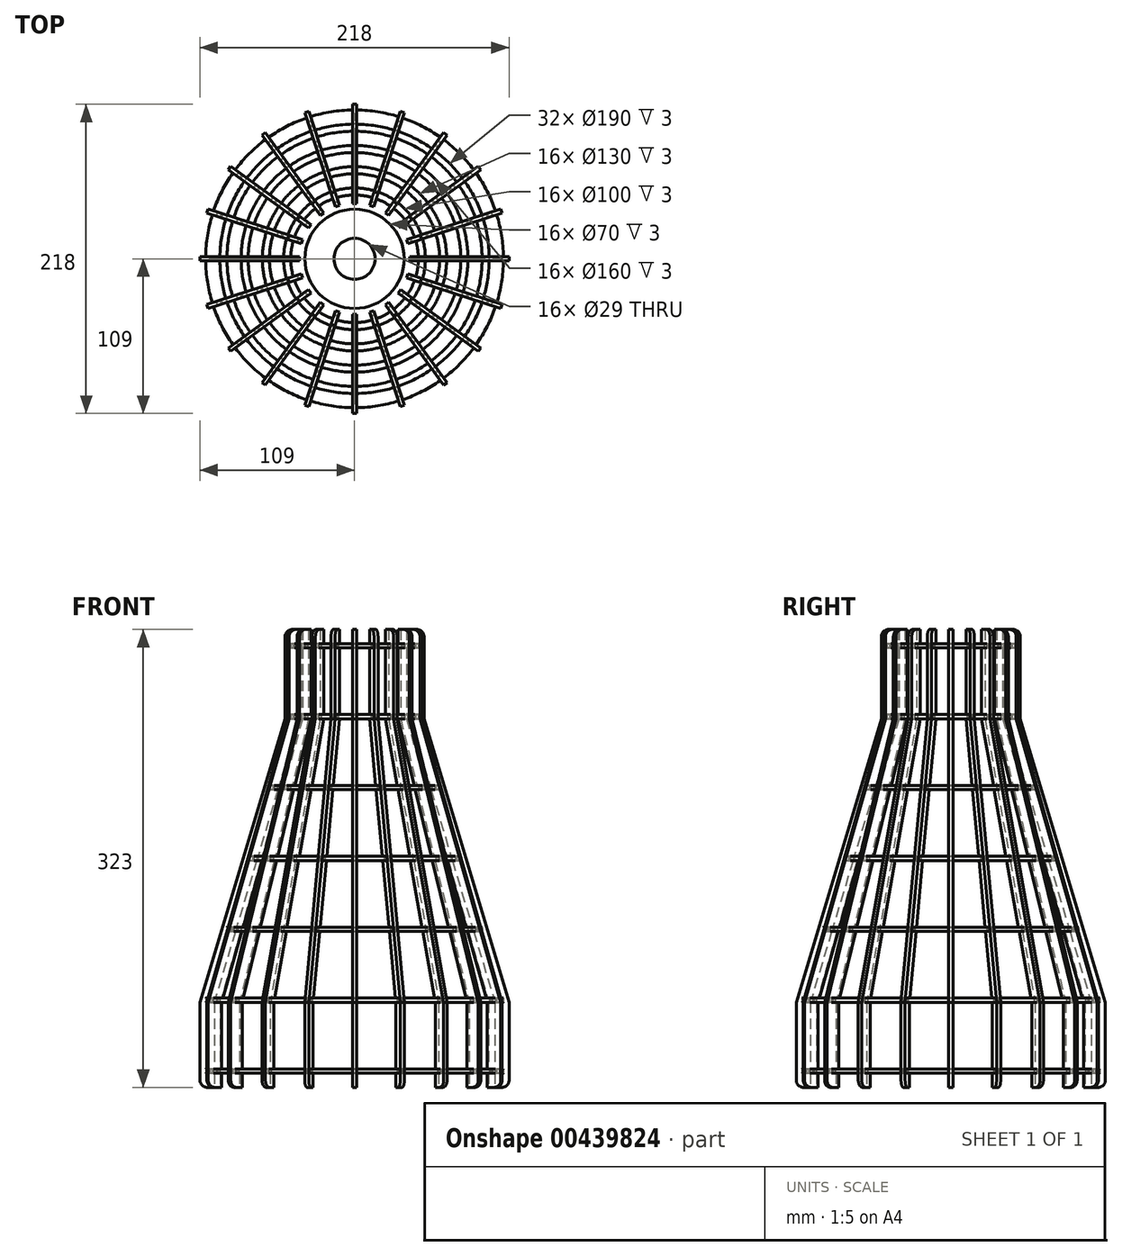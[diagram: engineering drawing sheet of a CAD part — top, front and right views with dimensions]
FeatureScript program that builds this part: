
annotation { "Feature Type Name" : "Feature", "Feature Type Description" : "" }
export const myFeature = defineFeature(function(context is Context, id is Id, definition is map)
    precondition{}
    {
        {
            var Q0;
            Q0=qCreatedBy(makeId("Top.planeOp"),FACE);
            cPlane(context, id + "F0", {"entities" : qUnion([Q0]), "cplaneType" : CPlaneType.OFFSET, "offset" : 50 * mm, "width" : 150 * mm, "height" : 150 * mm});
        }
        {
            var Q0;
            Q0=qCreatedBy(id+"F0.planeOp",FACE);
            cPlane(context, id + "F1", {"entities" : qUnion([Q0]), "cplaneType" : CPlaneType.OFFSET, "offset" : 50 * mm, "width" : 150 * mm, "height" : 150 * mm});
        }
        {
            var Q0;
            Q0=qCreatedBy(id+"F1.planeOp",FACE);
            cPlane(context, id + "F2", {"entities" : qUnion([Q0]), "cplaneType" : CPlaneType.OFFSET, "offset" : 50 * mm, "width" : 150 * mm, "height" : 150 * mm});
        }
        {
            var Q0;
            Q0=qCreatedBy(makeId("Top.planeOp"),FACE);
            cPlane(context, id + "F3", {"entities" : qUnion([Q0]), "cplaneType" : CPlaneType.OFFSET, "offset" : 50 * mm, "oppositeDirection" : true, "width" : 150 * mm, "height" : 150 * mm});
        }
        {
            var Q0;
            Q0=qCreatedBy(id+"F3.planeOp",FACE);
            cPlane(context, id + "F4", {"entities" : qUnion([Q0]), "cplaneType" : CPlaneType.OFFSET, "offset" : 50 * mm, "oppositeDirection" : true, "width" : 150 * mm, "height" : 150 * mm});
        }
        {
            var Q0;
            Q0=qCreatedBy(id+"F4.planeOp",FACE);
            cPlane(context, id + "F5", {"entities" : qUnion([Q0]), "cplaneType" : CPlaneType.OFFSET, "offset" : 50 * mm, "oppositeDirection" : true, "width" : 150 * mm, "height" : 150 * mm});
        }
        {
            var Q0;
            Q0=qCreatedBy(id+"F2.planeOp",FACE);
            var sketch = newSketch(context, id + "F6", { "sketchPlane" : qUnion([Q0])});
            skCircle(sketch, "E0", {"center": v(0, 0) * mm, "radius": 35 * mm});
            skArc(sketch, "E1", {"start": v(-44.98, -1.4) * mm, "mid": v(-44.45, -7.04) * mm, "end": v(-43.2, -12.57) * mm});
            skLineSegment(sketch, "E2", {"start": v(-44.98, 1.4) * mm, "end": v(-42, 1.4) * mm});
            skLineSegment(sketch, "E3", {"start": v(-42, 1.4) * mm, "end": v(-42, -1.4) * mm});
            skLineSegment(sketch, "E4", {"start": v(-42, -1.4) * mm, "end": v(-44.98, -1.4) * mm});
            skLineSegment(sketch, "E5.1.0", {"start": v(-43.2, -12.57) * mm, "end": v(-40.38, -11.65) * mm});
            skLineSegment(sketch, "E5.1.1", {"start": v(-40.38, -11.65) * mm, "end": v(-39.51, -14.31) * mm});
            skLineSegment(sketch, "E5.1.2", {"start": v(-39.51, -14.31) * mm, "end": v(-42.34, -15.23) * mm});
            skLineSegment(sketch, "E5.2.0", {"start": v(-37.21, -25.3) * mm, "end": v(-34.8, -23.55) * mm});
            skLineSegment(sketch, "E5.2.1", {"start": v(-34.8, -23.55) * mm, "end": v(-33.16, -25.82) * mm});
            skLineSegment(sketch, "E5.2.2", {"start": v(-33.16, -25.82) * mm, "end": v(-35.57, -27.57) * mm});
            skLineSegment(sketch, "E5.3.0", {"start": v(-27.57, -35.57) * mm, "end": v(-25.82, -33.16) * mm});
            skLineSegment(sketch, "E5.3.1", {"start": v(-25.82, -33.16) * mm, "end": v(-23.55, -34.8) * mm});
            skLineSegment(sketch, "E5.3.2", {"start": v(-23.55, -34.8) * mm, "end": v(-25.3, -37.21) * mm});
            skLineSegment(sketch, "E5.4.0", {"start": v(-15.23, -42.34) * mm, "end": v(-14.31, -39.51) * mm});
            skLineSegment(sketch, "E5.4.1", {"start": v(-14.31, -39.51) * mm, "end": v(-11.65, -40.38) * mm});
            skLineSegment(sketch, "E5.4.2", {"start": v(-11.65, -40.38) * mm, "end": v(-12.57, -43.2) * mm});
            skLineSegment(sketch, "E5.5.0", {"start": v(-1.4, -44.98) * mm, "end": v(-1.4, -42) * mm});
            skLineSegment(sketch, "E5.5.1", {"start": v(-1.4, -42) * mm, "end": v(1.4, -42) * mm});
            skLineSegment(sketch, "E5.5.2", {"start": v(1.4, -42) * mm, "end": v(1.4, -44.98) * mm});
            skLineSegment(sketch, "E5.6.0", {"start": v(12.57, -43.2) * mm, "end": v(11.65, -40.38) * mm});
            skLineSegment(sketch, "E5.6.1", {"start": v(11.65, -40.38) * mm, "end": v(14.31, -39.51) * mm});
            skLineSegment(sketch, "E5.6.2", {"start": v(14.31, -39.51) * mm, "end": v(15.23, -42.34) * mm});
            skLineSegment(sketch, "E5.7.0", {"start": v(25.3, -37.21) * mm, "end": v(23.55, -34.8) * mm});
            skLineSegment(sketch, "E5.7.1", {"start": v(23.55, -34.8) * mm, "end": v(25.82, -33.16) * mm});
            skLineSegment(sketch, "E5.7.2", {"start": v(25.82, -33.16) * mm, "end": v(27.57, -35.57) * mm});
            skLineSegment(sketch, "E5.8.0", {"start": v(35.57, -27.57) * mm, "end": v(33.16, -25.82) * mm});
            skLineSegment(sketch, "E5.8.1", {"start": v(33.16, -25.82) * mm, "end": v(34.8, -23.55) * mm});
            skLineSegment(sketch, "E5.8.2", {"start": v(34.8, -23.55) * mm, "end": v(37.21, -25.3) * mm});
            skLineSegment(sketch, "E5.9.0", {"start": v(42.34, -15.23) * mm, "end": v(39.51, -14.31) * mm});
            skLineSegment(sketch, "E5.9.1", {"start": v(39.51, -14.31) * mm, "end": v(40.38, -11.65) * mm});
            skLineSegment(sketch, "E5.9.2", {"start": v(40.38, -11.65) * mm, "end": v(43.2, -12.57) * mm});
            skLineSegment(sketch, "E5.10.0", {"start": v(44.98, -1.4) * mm, "end": v(42, -1.4) * mm});
            skLineSegment(sketch, "E5.10.1", {"start": v(42, -1.4) * mm, "end": v(42, 1.4) * mm});
            skLineSegment(sketch, "E5.10.2", {"start": v(42, 1.4) * mm, "end": v(44.98, 1.4) * mm});
            skLineSegment(sketch, "E5.11.0", {"start": v(43.2, 12.57) * mm, "end": v(40.38, 11.65) * mm});
            skLineSegment(sketch, "E5.11.1", {"start": v(40.38, 11.65) * mm, "end": v(39.51, 14.31) * mm});
            skLineSegment(sketch, "E5.11.2", {"start": v(39.51, 14.31) * mm, "end": v(42.34, 15.23) * mm});
            skLineSegment(sketch, "E5.12.0", {"start": v(37.21, 25.3) * mm, "end": v(34.8, 23.55) * mm});
            skLineSegment(sketch, "E5.12.1", {"start": v(34.8, 23.55) * mm, "end": v(33.16, 25.82) * mm});
            skLineSegment(sketch, "E5.12.2", {"start": v(33.16, 25.82) * mm, "end": v(35.57, 27.57) * mm});
            skLineSegment(sketch, "E5.13.0", {"start": v(27.57, 35.57) * mm, "end": v(25.82, 33.16) * mm});
            skLineSegment(sketch, "E5.13.1", {"start": v(25.82, 33.16) * mm, "end": v(23.55, 34.8) * mm});
            skLineSegment(sketch, "E5.13.2", {"start": v(23.55, 34.8) * mm, "end": v(25.3, 37.21) * mm});
            skLineSegment(sketch, "E5.14.0", {"start": v(15.23, 42.34) * mm, "end": v(14.31, 39.51) * mm});
            skLineSegment(sketch, "E5.14.1", {"start": v(14.31, 39.51) * mm, "end": v(11.65, 40.38) * mm});
            skLineSegment(sketch, "E5.14.2", {"start": v(11.65, 40.38) * mm, "end": v(12.57, 43.2) * mm});
            skLineSegment(sketch, "E5.15.0", {"start": v(1.4, 44.98) * mm, "end": v(1.4, 42) * mm});
            skLineSegment(sketch, "E5.15.1", {"start": v(1.4, 42) * mm, "end": v(-1.4, 42) * mm});
            skLineSegment(sketch, "E5.15.2", {"start": v(-1.4, 42) * mm, "end": v(-1.4, 44.98) * mm});
            skLineSegment(sketch, "E5.16.0", {"start": v(-12.57, 43.2) * mm, "end": v(-11.65, 40.38) * mm});
            skLineSegment(sketch, "E5.16.1", {"start": v(-11.65, 40.38) * mm, "end": v(-14.31, 39.51) * mm});
            skLineSegment(sketch, "E5.16.2", {"start": v(-14.31, 39.51) * mm, "end": v(-15.23, 42.34) * mm});
            skLineSegment(sketch, "E5.17.0", {"start": v(-25.3, 37.21) * mm, "end": v(-23.55, 34.8) * mm});
            skLineSegment(sketch, "E5.17.1", {"start": v(-23.55, 34.8) * mm, "end": v(-25.82, 33.16) * mm});
            skLineSegment(sketch, "E5.17.2", {"start": v(-25.82, 33.16) * mm, "end": v(-27.57, 35.57) * mm});
            skLineSegment(sketch, "E5.18.0", {"start": v(-35.57, 27.57) * mm, "end": v(-33.16, 25.82) * mm});
            skLineSegment(sketch, "E5.18.1", {"start": v(-33.16, 25.82) * mm, "end": v(-34.8, 23.55) * mm});
            skLineSegment(sketch, "E5.18.2", {"start": v(-34.8, 23.55) * mm, "end": v(-37.21, 25.3) * mm});
            skLineSegment(sketch, "E5.19.0", {"start": v(-42.34, 15.23) * mm, "end": v(-39.51, 14.31) * mm});
            skLineSegment(sketch, "E5.19.1", {"start": v(-39.51, 14.31) * mm, "end": v(-40.38, 11.65) * mm});
            skLineSegment(sketch, "E5.19.2", {"start": v(-40.38, 11.65) * mm, "end": v(-43.2, 12.57) * mm});
            skArc(sketch, "E6.trimOffspring", {"start": v(-42.34, -15.23) * mm, "mid": v(-40.1, -20.43) * mm, "end": v(-37.21, -25.3) * mm});
            skArc(sketch, "E7.trimOffspring", {"start": v(-43.2, 12.57) * mm, "mid": v(-44.45, 7.04) * mm, "end": v(-44.98, 1.4) * mm});
            skArc(sketch, "E8.trimOffspring", {"start": v(-37.21, 25.3) * mm, "mid": v(-40.1, 20.43) * mm, "end": v(-42.34, 15.23) * mm});
            skArc(sketch, "E9.trimOffspring", {"start": v(-27.57, 35.57) * mm, "mid": v(-31.82, 31.82) * mm, "end": v(-35.57, 27.57) * mm});
            skArc(sketch, "E10.trimOffspring", {"start": v(-15.23, 42.34) * mm, "mid": v(-20.43, 40.1) * mm, "end": v(-25.3, 37.21) * mm});
            skArc(sketch, "E11.trimOffspring", {"start": v(-1.4, 44.98) * mm, "mid": v(-7.04, 44.45) * mm, "end": v(-12.57, 43.2) * mm});
            skArc(sketch, "E12.trimOffspring", {"start": v(12.57, 43.2) * mm, "mid": v(7.04, 44.45) * mm, "end": v(1.4, 44.98) * mm});
            skArc(sketch, "E13.trimOffspring", {"start": v(25.3, 37.21) * mm, "mid": v(20.43, 40.1) * mm, "end": v(15.23, 42.34) * mm});
            skArc(sketch, "E14.trimOffspring", {"start": v(35.57, 27.57) * mm, "mid": v(31.82, 31.82) * mm, "end": v(27.57, 35.57) * mm});
            skArc(sketch, "E15.trimOffspring", {"start": v(42.34, 15.23) * mm, "mid": v(40.1, 20.43) * mm, "end": v(37.21, 25.3) * mm});
            skArc(sketch, "E16.trimOffspring", {"start": v(44.98, 1.4) * mm, "mid": v(44.45, 7.04) * mm, "end": v(43.2, 12.57) * mm});
            skArc(sketch, "E17.trimOffspring", {"start": v(43.2, -12.57) * mm, "mid": v(44.45, -7.04) * mm, "end": v(44.98, -1.4) * mm});
            skArc(sketch, "E18.trimOffspring", {"start": v(37.21, -25.3) * mm, "mid": v(40.1, -20.43) * mm, "end": v(42.34, -15.23) * mm});
            skArc(sketch, "E19.trimOffspring", {"start": v(27.57, -35.57) * mm, "mid": v(31.82, -31.82) * mm, "end": v(35.57, -27.57) * mm});
            skArc(sketch, "E20.trimOffspring", {"start": v(15.23, -42.34) * mm, "mid": v(20.43, -40.1) * mm, "end": v(25.3, -37.21) * mm});
            skArc(sketch, "E21.trimOffspring", {"start": v(1.4, -44.98) * mm, "mid": v(7.04, -44.45) * mm, "end": v(12.57, -43.2) * mm});
            skArc(sketch, "E22.trimOffspring", {"start": v(-12.57, -43.2) * mm, "mid": v(-7.04, -44.45) * mm, "end": v(-1.4, -44.98) * mm});
            skArc(sketch, "E23.trimOffspring", {"start": v(-25.3, -37.21) * mm, "mid": v(-20.43, -40.1) * mm, "end": v(-15.23, -42.34) * mm});
            skArc(sketch, "E24.trimOffspring", {"start": v(-35.57, -27.57) * mm, "mid": v(-31.82, -31.82) * mm, "end": v(-27.57, -35.57) * mm});
            skSolve(sketch);
        }
        {
            var Q0;
            Q0 = qSketchRegion(id + "F6", true);
            extrude(context, id + "F7", {"entities" : qUnion([Q0]), "depth" : 3 * mm});
        }
        {
            var Q0;
            Q0=qCreatedBy(id+"F1.planeOp",FACE);
            var sketch = newSketch(context, id + "F8", { "sketchPlane" : qUnion([Q0])});
            skCircle(sketch, "E25", {"center": v(0, 0) * mm, "radius": 14.5 * mm});
            skArc(sketch, "E26", {"start": v(-44.98, -1.4) * mm, "mid": v(-44.45, -7.04) * mm, "end": v(-43.2, -12.57) * mm});
            skLineSegment(sketch, "E27", {"start": v(-44.98, 1.4) * mm, "end": v(-41.98, 1.4) * mm});
            skLineSegment(sketch, "E28", {"start": v(-41.98, 1.4) * mm, "end": v(-41.98, -1.4) * mm});
            skLineSegment(sketch, "E29", {"start": v(-41.98, -1.4) * mm, "end": v(-44.98, -1.4) * mm});
            skLineSegment(sketch, "E30.1.0", {"start": v(-43.2, -12.57) * mm, "end": v(-40.36, -11.64) * mm});
            skLineSegment(sketch, "E30.1.1", {"start": v(-40.36, -11.64) * mm, "end": v(-39.5, -14.3) * mm});
            skLineSegment(sketch, "E30.1.2", {"start": v(-39.5, -14.3) * mm, "end": v(-42.34, -15.23) * mm});
            skLineSegment(sketch, "E30.2.0", {"start": v(-37.21, -25.3) * mm, "end": v(-34.78, -23.54) * mm});
            skLineSegment(sketch, "E30.2.1", {"start": v(-34.78, -23.54) * mm, "end": v(-33.14, -25.8) * mm});
            skLineSegment(sketch, "E30.2.2", {"start": v(-33.14, -25.8) * mm, "end": v(-35.57, -27.57) * mm});
            skLineSegment(sketch, "E31.3.3.0", {"start": v(-25.8, -33.14) * mm, "end": v(-23.54, -34.78) * mm});
            skLineSegment(sketch, "E31.6.3.0", {"start": v(-23.54, -34.78) * mm, "end": v(-25.3, -37.21) * mm});
            skLineSegment(sketch, "E31.8.3.0", {"start": v(-27.57, -35.57) * mm, "end": v(-25.8, -33.14) * mm});
            skLineSegment(sketch, "E31.3.4.0", {"start": v(-14.3, -39.5) * mm, "end": v(-11.64, -40.36) * mm});
            skLineSegment(sketch, "E31.6.4.0", {"start": v(-11.64, -40.36) * mm, "end": v(-12.57, -43.2) * mm});
            skLineSegment(sketch, "E31.8.4.0", {"start": v(-15.23, -42.34) * mm, "end": v(-14.3, -39.5) * mm});
            skLineSegment(sketch, "E31.3.5.0", {"start": v(-1.4, -41.98) * mm, "end": v(1.4, -41.98) * mm});
            skLineSegment(sketch, "E31.6.5.0", {"start": v(1.4, -41.98) * mm, "end": v(1.4, -44.98) * mm});
            skLineSegment(sketch, "E31.8.5.0", {"start": v(-1.4, -44.98) * mm, "end": v(-1.4, -41.98) * mm});
            skLineSegment(sketch, "E31.3.6.0", {"start": v(11.64, -40.36) * mm, "end": v(14.3, -39.5) * mm});
            skLineSegment(sketch, "E31.6.6.0", {"start": v(14.3, -39.5) * mm, "end": v(15.23, -42.34) * mm});
            skLineSegment(sketch, "E31.8.6.0", {"start": v(12.57, -43.2) * mm, "end": v(11.64, -40.36) * mm});
            skLineSegment(sketch, "E31.3.7.0", {"start": v(23.54, -34.78) * mm, "end": v(25.8, -33.14) * mm});
            skLineSegment(sketch, "E31.6.7.0", {"start": v(25.8, -33.14) * mm, "end": v(27.57, -35.57) * mm});
            skLineSegment(sketch, "E31.8.7.0", {"start": v(25.3, -37.21) * mm, "end": v(23.54, -34.78) * mm});
            skLineSegment(sketch, "E31.3.8.0", {"start": v(33.14, -25.8) * mm, "end": v(34.78, -23.54) * mm});
            skLineSegment(sketch, "E31.6.8.0", {"start": v(34.78, -23.54) * mm, "end": v(37.21, -25.3) * mm});
            skLineSegment(sketch, "E31.8.8.0", {"start": v(35.57, -27.57) * mm, "end": v(33.14, -25.8) * mm});
            skLineSegment(sketch, "E31.3.9.0", {"start": v(39.5, -14.3) * mm, "end": v(40.36, -11.64) * mm});
            skLineSegment(sketch, "E31.6.9.0", {"start": v(40.36, -11.64) * mm, "end": v(43.2, -12.57) * mm});
            skLineSegment(sketch, "E31.8.9.0", {"start": v(42.34, -15.23) * mm, "end": v(39.5, -14.3) * mm});
            skLineSegment(sketch, "E31.3.10.0", {"start": v(41.98, -1.4) * mm, "end": v(41.98, 1.4) * mm});
            skLineSegment(sketch, "E31.6.10.0", {"start": v(41.98, 1.4) * mm, "end": v(44.98, 1.4) * mm});
            skLineSegment(sketch, "E31.8.10.0", {"start": v(44.98, -1.4) * mm, "end": v(41.98, -1.4) * mm});
            skLineSegment(sketch, "E31.3.11.0", {"start": v(40.36, 11.64) * mm, "end": v(39.5, 14.3) * mm});
            skLineSegment(sketch, "E31.6.11.0", {"start": v(39.5, 14.3) * mm, "end": v(42.34, 15.23) * mm});
            skLineSegment(sketch, "E31.8.11.0", {"start": v(43.2, 12.57) * mm, "end": v(40.36, 11.64) * mm});
            skLineSegment(sketch, "E31.3.12.0", {"start": v(34.78, 23.54) * mm, "end": v(33.14, 25.8) * mm});
            skLineSegment(sketch, "E31.6.12.0", {"start": v(33.14, 25.8) * mm, "end": v(35.57, 27.57) * mm});
            skLineSegment(sketch, "E31.8.12.0", {"start": v(37.21, 25.3) * mm, "end": v(34.78, 23.54) * mm});
            skLineSegment(sketch, "E31.3.13.0", {"start": v(25.8, 33.14) * mm, "end": v(23.54, 34.78) * mm});
            skLineSegment(sketch, "E31.6.13.0", {"start": v(23.54, 34.78) * mm, "end": v(25.3, 37.21) * mm});
            skLineSegment(sketch, "E31.8.13.0", {"start": v(27.57, 35.57) * mm, "end": v(25.8, 33.14) * mm});
            skLineSegment(sketch, "E31.3.14.0", {"start": v(14.3, 39.5) * mm, "end": v(11.64, 40.36) * mm});
            skLineSegment(sketch, "E31.6.14.0", {"start": v(11.64, 40.36) * mm, "end": v(12.57, 43.2) * mm});
            skLineSegment(sketch, "E31.8.14.0", {"start": v(15.23, 42.34) * mm, "end": v(14.3, 39.5) * mm});
            skLineSegment(sketch, "E31.3.15.0", {"start": v(1.4, 41.98) * mm, "end": v(-1.4, 41.98) * mm});
            skLineSegment(sketch, "E31.6.15.0", {"start": v(-1.4, 41.98) * mm, "end": v(-1.4, 44.98) * mm});
            skLineSegment(sketch, "E31.8.15.0", {"start": v(1.4, 44.98) * mm, "end": v(1.4, 41.98) * mm});
            skLineSegment(sketch, "E31.3.16.0", {"start": v(-11.64, 40.36) * mm, "end": v(-14.3, 39.5) * mm});
            skLineSegment(sketch, "E31.6.16.0", {"start": v(-14.3, 39.5) * mm, "end": v(-15.23, 42.34) * mm});
            skLineSegment(sketch, "E31.8.16.0", {"start": v(-12.57, 43.2) * mm, "end": v(-11.64, 40.36) * mm});
            skLineSegment(sketch, "E31.3.17.0", {"start": v(-23.54, 34.78) * mm, "end": v(-25.8, 33.14) * mm});
            skLineSegment(sketch, "E31.6.17.0", {"start": v(-25.8, 33.14) * mm, "end": v(-27.57, 35.57) * mm});
            skLineSegment(sketch, "E31.8.17.0", {"start": v(-25.3, 37.21) * mm, "end": v(-23.54, 34.78) * mm});
            skLineSegment(sketch, "E31.3.18.0", {"start": v(-33.14, 25.8) * mm, "end": v(-34.78, 23.54) * mm});
            skLineSegment(sketch, "E31.6.18.0", {"start": v(-34.78, 23.54) * mm, "end": v(-37.21, 25.3) * mm});
            skLineSegment(sketch, "E31.8.18.0", {"start": v(-35.57, 27.57) * mm, "end": v(-33.14, 25.8) * mm});
            skLineSegment(sketch, "E31.3.19.0", {"start": v(-39.5, 14.3) * mm, "end": v(-40.36, 11.64) * mm});
            skLineSegment(sketch, "E31.6.19.0", {"start": v(-40.36, 11.64) * mm, "end": v(-43.2, 12.57) * mm});
            skLineSegment(sketch, "E31.8.19.0", {"start": v(-42.34, 15.23) * mm, "end": v(-39.5, 14.3) * mm});
            skArc(sketch, "E32.trimOffspring", {"start": v(-43.2, 12.57) * mm, "mid": v(-44.45, 7.04) * mm, "end": v(-44.98, 1.4) * mm});
            skArc(sketch, "E33.trimOffspring", {"start": v(-37.21, 25.3) * mm, "mid": v(-40.1, 20.43) * mm, "end": v(-42.34, 15.23) * mm});
            skArc(sketch, "E34.trimOffspring", {"start": v(-15.23, 42.34) * mm, "mid": v(-20.43, 40.1) * mm, "end": v(-25.3, 37.21) * mm});
            skArc(sketch, "E35.trimOffspring", {"start": v(-1.4, 44.98) * mm, "mid": v(-7.04, 44.45) * mm, "end": v(-12.57, 43.2) * mm});
            skArc(sketch, "E36.trimOffspring", {"start": v(12.57, 43.2) * mm, "mid": v(7.04, 44.45) * mm, "end": v(1.4, 44.98) * mm});
            skArc(sketch, "E37.trimOffspring", {"start": v(25.3, 37.21) * mm, "mid": v(20.43, 40.1) * mm, "end": v(15.23, 42.34) * mm});
            skArc(sketch, "E38.trimOffspring", {"start": v(35.57, 27.57) * mm, "mid": v(31.82, 31.82) * mm, "end": v(27.57, 35.57) * mm});
            skArc(sketch, "E39.trimOffspring", {"start": v(42.34, 15.23) * mm, "mid": v(40.1, 20.43) * mm, "end": v(37.21, 25.3) * mm});
            skArc(sketch, "E40.trimOffspring", {"start": v(44.98, 1.4) * mm, "mid": v(44.45, 7.04) * mm, "end": v(43.2, 12.57) * mm});
            skArc(sketch, "E41.trimOffspring", {"start": v(43.2, -12.57) * mm, "mid": v(44.45, -7.04) * mm, "end": v(44.98, -1.4) * mm});
            skArc(sketch, "E42.trimOffspring", {"start": v(37.21, -25.3) * mm, "mid": v(40.1, -20.43) * mm, "end": v(42.34, -15.23) * mm});
            skArc(sketch, "E43.trimOffspring", {"start": v(27.57, -35.57) * mm, "mid": v(31.82, -31.82) * mm, "end": v(35.57, -27.57) * mm});
            skArc(sketch, "E44.trimOffspring", {"start": v(15.23, -42.34) * mm, "mid": v(20.43, -40.1) * mm, "end": v(25.3, -37.21) * mm});
            skArc(sketch, "E45.trimOffspring", {"start": v(1.4, -44.98) * mm, "mid": v(7.04, -44.45) * mm, "end": v(12.57, -43.2) * mm});
            skArc(sketch, "E46.trimOffspring", {"start": v(-12.57, -43.2) * mm, "mid": v(-7.04, -44.45) * mm, "end": v(-1.4, -44.98) * mm});
            skArc(sketch, "E47.trimOffspring", {"start": v(-25.3, -37.21) * mm, "mid": v(-20.43, -40.1) * mm, "end": v(-15.23, -42.34) * mm});
            skArc(sketch, "E48.trimOffspring", {"start": v(-35.57, -27.57) * mm, "mid": v(-31.82, -31.82) * mm, "end": v(-27.57, -35.57) * mm});
            skArc(sketch, "E49.trimOffspring", {"start": v(-42.34, -15.23) * mm, "mid": v(-40.1, -20.43) * mm, "end": v(-37.21, -25.3) * mm});
            skArc(sketch, "E50.trimOffspring", {"start": v(-27.57, 35.57) * mm, "mid": v(-31.82, 31.82) * mm, "end": v(-35.57, 27.57) * mm});
            skSolve(sketch);
        }
        {
            var Q0;
            Q0 = qSketchRegion(id + "F8", true);
            extrude(context, id + "F9", {"entities" : qUnion([Q0]), "depth" : 3 * mm});
        }
        {
            var Q0;
            Q0=qCreatedBy(id+"F0.planeOp",FACE);
            var sketch = newSketch(context, id + "F10", { "sketchPlane" : qUnion([Q0])});
            skArc(sketch, "E51", {"start": v(-59.98, -1.4) * mm, "mid": v(-59.26, -9.39) * mm, "end": v(-57.48, -17.2) * mm});
            skCircle(sketch, "E52", {"center": v(0, 0) * mm, "radius": 50 * mm});
            skLineSegment(sketch, "E53", {"start": v(-59.98, 1.4) * mm, "end": v(-57, 1.4) * mm});
            skLineSegment(sketch, "E54", {"start": v(-57, 1.4) * mm, "end": v(-57, -1.4) * mm});
            skLineSegment(sketch, "E55", {"start": v(-57, -1.4) * mm, "end": v(-59.98, -1.4) * mm});
            skLineSegment(sketch, "E56.1.0", {"start": v(-57.48, -17.2) * mm, "end": v(-54.64, -16.28) * mm});
            skLineSegment(sketch, "E56.1.1", {"start": v(-54.64, -16.28) * mm, "end": v(-53.78, -18.95) * mm});
            skLineSegment(sketch, "E56.1.2", {"start": v(-53.78, -18.95) * mm, "end": v(-56.62, -19.87) * mm});
            skLineSegment(sketch, "E56.2.0", {"start": v(-49.35, -34.12) * mm, "end": v(-46.94, -32.37) * mm});
            skLineSegment(sketch, "E56.2.1", {"start": v(-46.94, -32.37) * mm, "end": v(-45.3, -34.64) * mm});
            skLineSegment(sketch, "E56.2.2", {"start": v(-45.3, -34.64) * mm, "end": v(-47.7, -36.4) * mm});
            skLineSegment(sketch, "E56.3.0", {"start": v(-36.4, -47.7) * mm, "end": v(-34.64, -45.3) * mm});
            skLineSegment(sketch, "E56.3.1", {"start": v(-34.64, -45.3) * mm, "end": v(-32.37, -46.94) * mm});
            skLineSegment(sketch, "E56.3.2", {"start": v(-32.37, -46.94) * mm, "end": v(-34.12, -49.35) * mm});
            skLineSegment(sketch, "E56.4.0", {"start": v(-19.87, -56.62) * mm, "end": v(-18.95, -53.78) * mm});
            skLineSegment(sketch, "E56.4.1", {"start": v(-18.95, -53.78) * mm, "end": v(-16.28, -54.64) * mm});
            skLineSegment(sketch, "E56.4.2", {"start": v(-16.28, -54.64) * mm, "end": v(-17.2, -57.48) * mm});
            skLineSegment(sketch, "E56.5.0", {"start": v(-1.4, -59.98) * mm, "end": v(-1.4, -57) * mm});
            skLineSegment(sketch, "E56.5.1", {"start": v(-1.4, -57) * mm, "end": v(1.4, -57) * mm});
            skLineSegment(sketch, "E56.5.2", {"start": v(1.4, -57) * mm, "end": v(1.4, -59.98) * mm});
            skLineSegment(sketch, "E56.6.0", {"start": v(17.2, -57.48) * mm, "end": v(16.28, -54.64) * mm});
            skLineSegment(sketch, "E56.6.1", {"start": v(16.28, -54.64) * mm, "end": v(18.95, -53.78) * mm});
            skLineSegment(sketch, "E56.6.2", {"start": v(18.95, -53.78) * mm, "end": v(19.87, -56.62) * mm});
            skLineSegment(sketch, "E56.7.0", {"start": v(34.12, -49.35) * mm, "end": v(32.37, -46.94) * mm});
            skLineSegment(sketch, "E56.7.1", {"start": v(32.37, -46.94) * mm, "end": v(34.64, -45.3) * mm});
            skLineSegment(sketch, "E56.7.2", {"start": v(34.64, -45.3) * mm, "end": v(36.4, -47.7) * mm});
            skLineSegment(sketch, "E56.8.0", {"start": v(47.7, -36.4) * mm, "end": v(45.3, -34.64) * mm});
            skLineSegment(sketch, "E56.8.1", {"start": v(45.3, -34.64) * mm, "end": v(46.94, -32.37) * mm});
            skLineSegment(sketch, "E56.8.2", {"start": v(46.94, -32.37) * mm, "end": v(49.35, -34.12) * mm});
            skLineSegment(sketch, "E56.9.0", {"start": v(56.62, -19.87) * mm, "end": v(53.78, -18.95) * mm});
            skLineSegment(sketch, "E56.9.1", {"start": v(53.78, -18.95) * mm, "end": v(54.64, -16.28) * mm});
            skLineSegment(sketch, "E56.9.2", {"start": v(54.64, -16.28) * mm, "end": v(57.48, -17.2) * mm});
            skLineSegment(sketch, "E56.10.0", {"start": v(59.98, -1.4) * mm, "end": v(57, -1.4) * mm});
            skLineSegment(sketch, "E56.10.1", {"start": v(57, -1.4) * mm, "end": v(57, 1.4) * mm});
            skLineSegment(sketch, "E56.10.2", {"start": v(57, 1.4) * mm, "end": v(59.98, 1.4) * mm});
            skLineSegment(sketch, "E56.11.0", {"start": v(57.48, 17.2) * mm, "end": v(54.64, 16.28) * mm});
            skLineSegment(sketch, "E56.11.1", {"start": v(54.64, 16.28) * mm, "end": v(53.78, 18.95) * mm});
            skLineSegment(sketch, "E56.11.2", {"start": v(53.78, 18.95) * mm, "end": v(56.62, 19.87) * mm});
            skLineSegment(sketch, "E56.12.0", {"start": v(49.35, 34.12) * mm, "end": v(46.94, 32.37) * mm});
            skLineSegment(sketch, "E56.12.1", {"start": v(46.94, 32.37) * mm, "end": v(45.3, 34.64) * mm});
            skLineSegment(sketch, "E56.12.2", {"start": v(45.3, 34.64) * mm, "end": v(47.7, 36.4) * mm});
            skLineSegment(sketch, "E56.13.0", {"start": v(36.4, 47.7) * mm, "end": v(34.64, 45.3) * mm});
            skLineSegment(sketch, "E56.13.1", {"start": v(34.64, 45.3) * mm, "end": v(32.37, 46.94) * mm});
            skLineSegment(sketch, "E56.13.2", {"start": v(32.37, 46.94) * mm, "end": v(34.12, 49.35) * mm});
            skLineSegment(sketch, "E56.14.0", {"start": v(19.87, 56.62) * mm, "end": v(18.95, 53.78) * mm});
            skLineSegment(sketch, "E56.14.1", {"start": v(18.95, 53.78) * mm, "end": v(16.28, 54.64) * mm});
            skLineSegment(sketch, "E56.14.2", {"start": v(16.28, 54.64) * mm, "end": v(17.2, 57.48) * mm});
            skLineSegment(sketch, "E56.15.0", {"start": v(1.4, 59.98) * mm, "end": v(1.4, 57) * mm});
            skLineSegment(sketch, "E56.15.1", {"start": v(1.4, 57) * mm, "end": v(-1.4, 57) * mm});
            skLineSegment(sketch, "E56.15.2", {"start": v(-1.4, 57) * mm, "end": v(-1.4, 59.98) * mm});
            skLineSegment(sketch, "E56.16.0", {"start": v(-17.2, 57.48) * mm, "end": v(-16.28, 54.64) * mm});
            skLineSegment(sketch, "E56.16.1", {"start": v(-16.28, 54.64) * mm, "end": v(-18.95, 53.78) * mm});
            skLineSegment(sketch, "E56.16.2", {"start": v(-18.95, 53.78) * mm, "end": v(-19.87, 56.62) * mm});
            skLineSegment(sketch, "E56.17.0", {"start": v(-34.12, 49.35) * mm, "end": v(-32.37, 46.94) * mm});
            skLineSegment(sketch, "E56.17.1", {"start": v(-32.37, 46.94) * mm, "end": v(-34.64, 45.3) * mm});
            skLineSegment(sketch, "E56.17.2", {"start": v(-34.64, 45.3) * mm, "end": v(-36.4, 47.7) * mm});
            skLineSegment(sketch, "E56.18.0", {"start": v(-47.7, 36.4) * mm, "end": v(-45.3, 34.64) * mm});
            skLineSegment(sketch, "E56.18.1", {"start": v(-45.3, 34.64) * mm, "end": v(-46.94, 32.37) * mm});
            skLineSegment(sketch, "E56.18.2", {"start": v(-46.94, 32.37) * mm, "end": v(-49.35, 34.12) * mm});
            skLineSegment(sketch, "E56.19.0", {"start": v(-56.62, 19.87) * mm, "end": v(-53.78, 18.95) * mm});
            skLineSegment(sketch, "E56.19.1", {"start": v(-53.78, 18.95) * mm, "end": v(-54.64, 16.28) * mm});
            skLineSegment(sketch, "E56.19.2", {"start": v(-54.64, 16.28) * mm, "end": v(-57.48, 17.2) * mm});
            skArc(sketch, "E57.trimOffspring", {"start": v(-57.48, 17.2) * mm, "mid": v(-59.26, 9.39) * mm, "end": v(-59.98, 1.4) * mm});
            skArc(sketch, "E58.trimOffspring", {"start": v(-56.62, -19.87) * mm, "mid": v(-53.46, -27.24) * mm, "end": v(-49.35, -34.12) * mm});
            skArc(sketch, "E59.trimOffspring", {"start": v(-47.7, -36.4) * mm, "mid": v(-42.43, -42.43) * mm, "end": v(-36.4, -47.7) * mm});
            skArc(sketch, "E60.trimOffspring", {"start": v(-34.12, -49.35) * mm, "mid": v(-27.24, -53.46) * mm, "end": v(-19.87, -56.62) * mm});
            skArc(sketch, "E61.trimOffspring", {"start": v(-17.2, -57.48) * mm, "mid": v(-9.39, -59.26) * mm, "end": v(-1.4, -59.98) * mm});
            skArc(sketch, "E62.trimOffspring", {"start": v(1.4, -59.98) * mm, "mid": v(9.39, -59.26) * mm, "end": v(17.2, -57.48) * mm});
            skArc(sketch, "E63.trimOffspring", {"start": v(19.87, -56.62) * mm, "mid": v(27.24, -53.46) * mm, "end": v(34.12, -49.35) * mm});
            skArc(sketch, "E64.trimOffspring", {"start": v(36.4, -47.7) * mm, "mid": v(42.43, -42.43) * mm, "end": v(47.7, -36.4) * mm});
            skArc(sketch, "E65.trimOffspring", {"start": v(49.35, -34.12) * mm, "mid": v(53.46, -27.24) * mm, "end": v(56.62, -19.87) * mm});
            skArc(sketch, "E66.trimOffspring", {"start": v(57.48, -17.2) * mm, "mid": v(59.26, -9.39) * mm, "end": v(59.98, -1.4) * mm});
            skArc(sketch, "E67.trimOffspring", {"start": v(59.98, 1.4) * mm, "mid": v(59.26, 9.39) * mm, "end": v(57.48, 17.2) * mm});
            skArc(sketch, "E68.trimOffspring", {"start": v(56.62, 19.87) * mm, "mid": v(53.46, 27.24) * mm, "end": v(49.35, 34.12) * mm});
            skArc(sketch, "E69.trimOffspring", {"start": v(47.7, 36.4) * mm, "mid": v(42.43, 42.43) * mm, "end": v(36.4, 47.7) * mm});
            skArc(sketch, "E70.trimOffspring", {"start": v(34.12, 49.35) * mm, "mid": v(27.24, 53.46) * mm, "end": v(19.87, 56.62) * mm});
            skArc(sketch, "E71.trimOffspring", {"start": v(17.2, 57.48) * mm, "mid": v(9.39, 59.26) * mm, "end": v(1.4, 59.98) * mm});
            skArc(sketch, "E72.trimOffspring", {"start": v(-1.4, 59.98) * mm, "mid": v(-9.39, 59.26) * mm, "end": v(-17.2, 57.48) * mm});
            skArc(sketch, "E73.trimOffspring", {"start": v(-19.87, 56.62) * mm, "mid": v(-27.24, 53.46) * mm, "end": v(-34.12, 49.35) * mm});
            skArc(sketch, "E74.trimOffspring", {"start": v(-36.4, 47.7) * mm, "mid": v(-42.43, 42.43) * mm, "end": v(-47.7, 36.4) * mm});
            skArc(sketch, "E75.trimOffspring", {"start": v(-49.35, 34.12) * mm, "mid": v(-53.46, 27.24) * mm, "end": v(-56.62, 19.87) * mm});
            skSolve(sketch);
        }
        {
            var Q0;
            Q0 = qSketchRegion(id + "F10", true);
            extrude(context, id + "F11", {"entities" : qUnion([Q0]), "depth" : 3 * mm});
        }
        {
            var Q0;
            Q0=qCreatedBy(makeId("Top.planeOp"),FACE);
            var sketch = newSketch(context, id + "F12", { "sketchPlane" : qUnion([Q0])});
            skCircle(sketch, "E76", {"center": v(0, 0) * mm, "radius": 65 * mm});
            skArc(sketch, "E77", {"start": v(-74.99, -1.4) * mm, "mid": v(-74.08, -11.73) * mm, "end": v(-71.75, -21.84) * mm});
            skLineSegment(sketch, "E78", {"start": v(-75, 1.4) * mm, "end": v(-72, 1.4) * mm});
            skLineSegment(sketch, "E79", {"start": v(-72, 1.4) * mm, "end": v(-72, -1.4) * mm});
            skLineSegment(sketch, "E80", {"start": v(-72, -1.4) * mm, "end": v(-75, -1.4) * mm});
            skLineSegment(sketch, "E81.1.0", {"start": v(-71.76, -21.84) * mm, "end": v(-68.9, -20.92) * mm});
            skLineSegment(sketch, "E81.1.1", {"start": v(-68.9, -20.92) * mm, "end": v(-68.04, -23.58) * mm});
            skLineSegment(sketch, "E81.1.2", {"start": v(-68.04, -23.58) * mm, "end": v(-70.9, -24.5) * mm});
            skLineSegment(sketch, "E81.2.0", {"start": v(-61.5, -42.95) * mm, "end": v(-59.07, -41.19) * mm});
            skLineSegment(sketch, "E81.2.1", {"start": v(-59.07, -41.19) * mm, "end": v(-57.43, -43.45) * mm});
            skLineSegment(sketch, "E81.2.2", {"start": v(-57.43, -43.45) * mm, "end": v(-59.85, -45.22) * mm});
            skLineSegment(sketch, "E81.3.0", {"start": v(-45.22, -59.85) * mm, "end": v(-43.45, -57.43) * mm});
            skLineSegment(sketch, "E81.3.1", {"start": v(-43.45, -57.43) * mm, "end": v(-41.19, -59.07) * mm});
            skLineSegment(sketch, "E81.3.2", {"start": v(-41.19, -59.07) * mm, "end": v(-42.95, -61.5) * mm});
            skLineSegment(sketch, "E81.4.0", {"start": v(-24.5, -70.9) * mm, "end": v(-23.58, -68.04) * mm});
            skLineSegment(sketch, "E81.4.1", {"start": v(-23.58, -68.04) * mm, "end": v(-20.92, -68.9) * mm});
            skLineSegment(sketch, "E81.4.2", {"start": v(-20.92, -68.9) * mm, "end": v(-21.84, -71.76) * mm});
            skLineSegment(sketch, "E81.5.0", {"start": v(-1.4, -75) * mm, "end": v(-1.4, -72) * mm});
            skLineSegment(sketch, "E81.5.1", {"start": v(-1.4, -72) * mm, "end": v(1.4, -72) * mm});
            skLineSegment(sketch, "E81.5.2", {"start": v(1.4, -72) * mm, "end": v(1.4, -75) * mm});
            skLineSegment(sketch, "E81.6.0", {"start": v(21.84, -71.76) * mm, "end": v(20.92, -68.9) * mm});
            skLineSegment(sketch, "E81.6.1", {"start": v(20.92, -68.9) * mm, "end": v(23.58, -68.04) * mm});
            skLineSegment(sketch, "E81.6.2", {"start": v(23.58, -68.04) * mm, "end": v(24.5, -70.9) * mm});
            skLineSegment(sketch, "E81.7.0", {"start": v(42.95, -61.5) * mm, "end": v(41.19, -59.07) * mm});
            skLineSegment(sketch, "E81.7.1", {"start": v(41.19, -59.07) * mm, "end": v(43.45, -57.43) * mm});
            skLineSegment(sketch, "E81.7.2", {"start": v(43.45, -57.43) * mm, "end": v(45.22, -59.85) * mm});
            skLineSegment(sketch, "E81.8.0", {"start": v(59.85, -45.22) * mm, "end": v(57.43, -43.45) * mm});
            skLineSegment(sketch, "E81.8.1", {"start": v(57.43, -43.45) * mm, "end": v(59.07, -41.19) * mm});
            skLineSegment(sketch, "E81.8.2", {"start": v(59.07, -41.19) * mm, "end": v(61.5, -42.95) * mm});
            skLineSegment(sketch, "E81.9.0", {"start": v(70.9, -24.5) * mm, "end": v(68.04, -23.58) * mm});
            skLineSegment(sketch, "E81.9.1", {"start": v(68.04, -23.58) * mm, "end": v(68.9, -20.92) * mm});
            skLineSegment(sketch, "E81.9.2", {"start": v(68.9, -20.92) * mm, "end": v(71.76, -21.84) * mm});
            skLineSegment(sketch, "E81.10.0", {"start": v(75, -1.4) * mm, "end": v(72, -1.4) * mm});
            skLineSegment(sketch, "E81.10.1", {"start": v(72, -1.4) * mm, "end": v(72, 1.4) * mm});
            skLineSegment(sketch, "E81.10.2", {"start": v(72, 1.4) * mm, "end": v(75, 1.4) * mm});
            skLineSegment(sketch, "E81.11.0", {"start": v(71.76, 21.84) * mm, "end": v(68.9, 20.92) * mm});
            skLineSegment(sketch, "E81.11.1", {"start": v(68.9, 20.92) * mm, "end": v(68.04, 23.58) * mm});
            skLineSegment(sketch, "E81.11.2", {"start": v(68.04, 23.58) * mm, "end": v(70.9, 24.5) * mm});
            skLineSegment(sketch, "E81.12.0", {"start": v(61.5, 42.95) * mm, "end": v(59.07, 41.19) * mm});
            skLineSegment(sketch, "E81.12.1", {"start": v(59.07, 41.19) * mm, "end": v(57.43, 43.45) * mm});
            skLineSegment(sketch, "E81.12.2", {"start": v(57.43, 43.45) * mm, "end": v(59.85, 45.22) * mm});
            skLineSegment(sketch, "E81.13.0", {"start": v(45.22, 59.85) * mm, "end": v(43.45, 57.43) * mm});
            skLineSegment(sketch, "E81.13.1", {"start": v(43.45, 57.43) * mm, "end": v(41.19, 59.07) * mm});
            skLineSegment(sketch, "E81.13.2", {"start": v(41.19, 59.07) * mm, "end": v(42.95, 61.5) * mm});
            skLineSegment(sketch, "E81.14.0", {"start": v(24.5, 70.9) * mm, "end": v(23.58, 68.04) * mm});
            skLineSegment(sketch, "E81.14.1", {"start": v(23.58, 68.04) * mm, "end": v(20.92, 68.9) * mm});
            skLineSegment(sketch, "E81.14.2", {"start": v(20.92, 68.9) * mm, "end": v(21.84, 71.76) * mm});
            skLineSegment(sketch, "E81.15.0", {"start": v(1.4, 75) * mm, "end": v(1.4, 72) * mm});
            skLineSegment(sketch, "E81.15.1", {"start": v(1.4, 72) * mm, "end": v(-1.4, 72) * mm});
            skLineSegment(sketch, "E81.15.2", {"start": v(-1.4, 72) * mm, "end": v(-1.4, 75) * mm});
            skLineSegment(sketch, "E81.16.0", {"start": v(-21.84, 71.76) * mm, "end": v(-20.92, 68.9) * mm});
            skLineSegment(sketch, "E81.16.1", {"start": v(-20.92, 68.9) * mm, "end": v(-23.58, 68.04) * mm});
            skLineSegment(sketch, "E81.16.2", {"start": v(-23.58, 68.04) * mm, "end": v(-24.5, 70.9) * mm});
            skLineSegment(sketch, "E81.17.0", {"start": v(-42.95, 61.5) * mm, "end": v(-41.19, 59.07) * mm});
            skLineSegment(sketch, "E81.17.1", {"start": v(-41.19, 59.07) * mm, "end": v(-43.45, 57.43) * mm});
            skLineSegment(sketch, "E81.17.2", {"start": v(-43.45, 57.43) * mm, "end": v(-45.22, 59.85) * mm});
            skLineSegment(sketch, "E81.18.0", {"start": v(-59.85, 45.22) * mm, "end": v(-57.43, 43.45) * mm});
            skLineSegment(sketch, "E81.18.1", {"start": v(-57.43, 43.45) * mm, "end": v(-59.07, 41.19) * mm});
            skLineSegment(sketch, "E81.18.2", {"start": v(-59.07, 41.19) * mm, "end": v(-61.5, 42.95) * mm});
            skLineSegment(sketch, "E81.19.0", {"start": v(-70.9, 24.5) * mm, "end": v(-68.04, 23.58) * mm});
            skLineSegment(sketch, "E81.19.1", {"start": v(-68.04, 23.58) * mm, "end": v(-68.9, 20.92) * mm});
            skLineSegment(sketch, "E81.19.2", {"start": v(-68.9, 20.92) * mm, "end": v(-71.76, 21.84) * mm});
            skArc(sketch, "E82.trimOffspring", {"start": v(-61.49, 42.94) * mm, "mid": v(-66.83, 34.05) * mm, "end": v(-70.88, 24.5) * mm});
            skArc(sketch, "E83.trimOffspring", {"start": v(-71.75, 21.84) * mm, "mid": v(-74.08, 11.73) * mm, "end": v(-74.99, 1.4) * mm});
            skArc(sketch, "E84.trimOffspring", {"start": v(-45.2, 59.84) * mm, "mid": v(-53.03, 53.03) * mm, "end": v(-59.84, 45.2) * mm});
            skArc(sketch, "E85.trimOffspring", {"start": v(-24.5, 70.88) * mm, "mid": v(-34.05, 66.83) * mm, "end": v(-42.94, 61.49) * mm});
            skArc(sketch, "E86.trimOffspring", {"start": v(-1.4, 74.99) * mm, "mid": v(-11.73, 74.08) * mm, "end": v(-21.84, 71.75) * mm});
            skArc(sketch, "E87.trimOffspring", {"start": v(21.84, 71.75) * mm, "mid": v(11.73, 74.08) * mm, "end": v(1.4, 74.99) * mm});
            skArc(sketch, "E88.trimOffspring", {"start": v(42.94, 61.49) * mm, "mid": v(34.05, 66.83) * mm, "end": v(24.5, 70.88) * mm});
            skArc(sketch, "E89.trimOffspring", {"start": v(59.84, 45.2) * mm, "mid": v(53.03, 53.03) * mm, "end": v(45.2, 59.84) * mm});
            skArc(sketch, "E90.trimOffspring", {"start": v(70.88, 24.5) * mm, "mid": v(66.83, 34.05) * mm, "end": v(61.49, 42.94) * mm});
            skArc(sketch, "E91.trimOffspring", {"start": v(74.99, 1.4) * mm, "mid": v(74.08, 11.73) * mm, "end": v(71.75, 21.84) * mm});
            skArc(sketch, "E92.trimOffspring", {"start": v(71.75, -21.84) * mm, "mid": v(74.08, -11.73) * mm, "end": v(74.99, -1.4) * mm});
            skArc(sketch, "E93.trimOffspring", {"start": v(61.49, -42.94) * mm, "mid": v(66.83, -34.05) * mm, "end": v(70.88, -24.5) * mm});
            skArc(sketch, "E94.trimOffspring", {"start": v(45.2, -59.84) * mm, "mid": v(53.03, -53.03) * mm, "end": v(59.84, -45.2) * mm});
            skArc(sketch, "E95.trimOffspring", {"start": v(24.5, -70.88) * mm, "mid": v(34.05, -66.83) * mm, "end": v(42.94, -61.49) * mm});
            skArc(sketch, "E96.trimOffspring", {"start": v(1.4, -74.99) * mm, "mid": v(11.73, -74.08) * mm, "end": v(21.84, -71.75) * mm});
            skArc(sketch, "E97.trimOffspring", {"start": v(-21.84, -71.75) * mm, "mid": v(-11.73, -74.08) * mm, "end": v(-1.4, -74.99) * mm});
            skArc(sketch, "E98.trimOffspring", {"start": v(-42.94, -61.49) * mm, "mid": v(-34.05, -66.83) * mm, "end": v(-24.5, -70.88) * mm});
            skArc(sketch, "E99.trimOffspring", {"start": v(-59.84, -45.2) * mm, "mid": v(-53.03, -53.03) * mm, "end": v(-45.2, -59.84) * mm});
            skArc(sketch, "E100.trimOffspring", {"start": v(-70.88, -24.5) * mm, "mid": v(-66.83, -34.05) * mm, "end": v(-61.49, -42.94) * mm});
            skSolve(sketch);
        }
        {
            var Q0;
            Q0 = qSketchRegion(id + "F12", true);
            extrude(context, id + "F13", {"entities" : qUnion([Q0]), "depth" : 3 * mm});
        }
        {
            var Q0;
            Q0=qCreatedBy(id+"F3.planeOp",FACE);
            var sketch = newSketch(context, id + "F14", { "sketchPlane" : qUnion([Q0])});
            skCircle(sketch, "E101", {"center": v(0, 0) * mm, "radius": 80 * mm});
            skArc(sketch, "E102", {"start": v(-89.99, -1.4) * mm, "mid": v(-88.9, -14.08) * mm, "end": v(-86.02, -26.48) * mm});
            skLineSegment(sketch, "E103", {"start": v(-90, 1.4) * mm, "end": v(-87, 1.4) * mm});
            skLineSegment(sketch, "E104", {"start": v(-87, 1.4) * mm, "end": v(-87, -1.4) * mm});
            skLineSegment(sketch, "E105", {"start": v(-87, -1.4) * mm, "end": v(-90, -1.4) * mm});
            skLineSegment(sketch, "E106.1.0", {"start": v(-86.03, -26.48) * mm, "end": v(-83.17, -25.55) * mm});
            skLineSegment(sketch, "E106.1.1", {"start": v(-83.17, -25.55) * mm, "end": v(-82.3, -28.22) * mm});
            skLineSegment(sketch, "E106.1.2", {"start": v(-82.3, -28.22) * mm, "end": v(-85.16, -29.14) * mm});
            skLineSegment(sketch, "E106.2.0", {"start": v(-73.63, -51.77) * mm, "end": v(-71.2, -50) * mm});
            skLineSegment(sketch, "E106.2.1", {"start": v(-71.2, -50) * mm, "end": v(-69.56, -52.27) * mm});
            skLineSegment(sketch, "E106.2.2", {"start": v(-69.56, -52.27) * mm, "end": v(-71.99, -54.03) * mm});
            skLineSegment(sketch, "E106.3.0", {"start": v(-54.03, -71.99) * mm, "end": v(-52.27, -69.56) * mm});
            skLineSegment(sketch, "E106.3.1", {"start": v(-52.27, -69.56) * mm, "end": v(-50, -71.2) * mm});
            skLineSegment(sketch, "E106.3.2", {"start": v(-50, -71.2) * mm, "end": v(-51.77, -73.63) * mm});
            skLineSegment(sketch, "E106.4.0", {"start": v(-29.14, -85.16) * mm, "end": v(-28.22, -82.3) * mm});
            skLineSegment(sketch, "E106.4.1", {"start": v(-28.22, -82.3) * mm, "end": v(-25.55, -83.17) * mm});
            skLineSegment(sketch, "E106.4.2", {"start": v(-25.55, -83.17) * mm, "end": v(-26.48, -86.03) * mm});
            skLineSegment(sketch, "E106.5.0", {"start": v(-1.4, -90) * mm, "end": v(-1.4, -87) * mm});
            skLineSegment(sketch, "E106.5.1", {"start": v(-1.4, -87) * mm, "end": v(1.4, -87) * mm});
            skLineSegment(sketch, "E106.5.2", {"start": v(1.4, -87) * mm, "end": v(1.4, -90) * mm});
            skLineSegment(sketch, "E106.6.0", {"start": v(26.48, -86.03) * mm, "end": v(25.55, -83.17) * mm});
            skLineSegment(sketch, "E106.6.1", {"start": v(25.55, -83.17) * mm, "end": v(28.22, -82.3) * mm});
            skLineSegment(sketch, "E106.6.2", {"start": v(28.22, -82.3) * mm, "end": v(29.14, -85.16) * mm});
            skLineSegment(sketch, "E106.7.0", {"start": v(51.77, -73.63) * mm, "end": v(50, -71.2) * mm});
            skLineSegment(sketch, "E106.7.1", {"start": v(50, -71.2) * mm, "end": v(52.27, -69.56) * mm});
            skLineSegment(sketch, "E106.7.2", {"start": v(52.27, -69.56) * mm, "end": v(54.03, -71.99) * mm});
            skLineSegment(sketch, "E106.8.0", {"start": v(71.99, -54.03) * mm, "end": v(69.56, -52.27) * mm});
            skLineSegment(sketch, "E106.8.1", {"start": v(69.56, -52.27) * mm, "end": v(71.2, -50) * mm});
            skLineSegment(sketch, "E106.8.2", {"start": v(71.2, -50) * mm, "end": v(73.63, -51.77) * mm});
            skLineSegment(sketch, "E106.9.0", {"start": v(85.16, -29.14) * mm, "end": v(82.3, -28.22) * mm});
            skLineSegment(sketch, "E106.9.1", {"start": v(82.3, -28.22) * mm, "end": v(83.17, -25.55) * mm});
            skLineSegment(sketch, "E106.9.2", {"start": v(83.17, -25.55) * mm, "end": v(86.03, -26.48) * mm});
            skLineSegment(sketch, "E106.10.0", {"start": v(90, -1.4) * mm, "end": v(87, -1.4) * mm});
            skLineSegment(sketch, "E106.10.1", {"start": v(87, -1.4) * mm, "end": v(87, 1.4) * mm});
            skLineSegment(sketch, "E106.10.2", {"start": v(87, 1.4) * mm, "end": v(90, 1.4) * mm});
            skLineSegment(sketch, "E106.11.0", {"start": v(86.03, 26.48) * mm, "end": v(83.17, 25.55) * mm});
            skLineSegment(sketch, "E106.11.1", {"start": v(83.17, 25.55) * mm, "end": v(82.3, 28.22) * mm});
            skLineSegment(sketch, "E106.11.2", {"start": v(82.3, 28.22) * mm, "end": v(85.16, 29.14) * mm});
            skLineSegment(sketch, "E106.12.0", {"start": v(73.63, 51.77) * mm, "end": v(71.2, 50) * mm});
            skLineSegment(sketch, "E106.12.1", {"start": v(71.2, 50) * mm, "end": v(69.56, 52.27) * mm});
            skLineSegment(sketch, "E106.12.2", {"start": v(69.56, 52.27) * mm, "end": v(71.99, 54.03) * mm});
            skLineSegment(sketch, "E106.13.0", {"start": v(54.03, 71.99) * mm, "end": v(52.27, 69.56) * mm});
            skLineSegment(sketch, "E106.13.1", {"start": v(52.27, 69.56) * mm, "end": v(50, 71.2) * mm});
            skLineSegment(sketch, "E106.13.2", {"start": v(50, 71.2) * mm, "end": v(51.77, 73.63) * mm});
            skLineSegment(sketch, "E106.14.0", {"start": v(29.14, 85.16) * mm, "end": v(28.22, 82.3) * mm});
            skLineSegment(sketch, "E106.14.1", {"start": v(28.22, 82.3) * mm, "end": v(25.55, 83.17) * mm});
            skLineSegment(sketch, "E106.14.2", {"start": v(25.55, 83.17) * mm, "end": v(26.48, 86.03) * mm});
            skLineSegment(sketch, "E106.15.0", {"start": v(1.4, 90) * mm, "end": v(1.4, 87) * mm});
            skLineSegment(sketch, "E106.15.1", {"start": v(1.4, 87) * mm, "end": v(-1.4, 87) * mm});
            skLineSegment(sketch, "E106.15.2", {"start": v(-1.4, 87) * mm, "end": v(-1.4, 90) * mm});
            skLineSegment(sketch, "E106.16.0", {"start": v(-26.48, 86.03) * mm, "end": v(-25.55, 83.17) * mm});
            skLineSegment(sketch, "E106.16.1", {"start": v(-25.55, 83.17) * mm, "end": v(-28.22, 82.3) * mm});
            skLineSegment(sketch, "E106.16.2", {"start": v(-28.22, 82.3) * mm, "end": v(-29.14, 85.16) * mm});
            skLineSegment(sketch, "E106.17.0", {"start": v(-51.77, 73.63) * mm, "end": v(-50, 71.2) * mm});
            skLineSegment(sketch, "E106.17.1", {"start": v(-50, 71.2) * mm, "end": v(-52.27, 69.56) * mm});
            skLineSegment(sketch, "E106.17.2", {"start": v(-52.27, 69.56) * mm, "end": v(-54.03, 71.99) * mm});
            skLineSegment(sketch, "E106.18.0", {"start": v(-71.99, 54.03) * mm, "end": v(-69.56, 52.27) * mm});
            skLineSegment(sketch, "E106.18.1", {"start": v(-69.56, 52.27) * mm, "end": v(-71.2, 50) * mm});
            skLineSegment(sketch, "E106.18.2", {"start": v(-71.2, 50) * mm, "end": v(-73.63, 51.77) * mm});
            skLineSegment(sketch, "E106.19.0", {"start": v(-85.16, 29.14) * mm, "end": v(-82.3, 28.22) * mm});
            skLineSegment(sketch, "E106.19.1", {"start": v(-82.3, 28.22) * mm, "end": v(-83.17, 25.55) * mm});
            skLineSegment(sketch, "E106.19.2", {"start": v(-83.17, 25.55) * mm, "end": v(-86.03, 26.48) * mm});
            skArc(sketch, "E107.trimOffspring", {"start": v(-86.02, 26.48) * mm, "mid": v(-88.9, 14.08) * mm, "end": v(-89.99, 1.4) * mm});
            skArc(sketch, "E108.trimOffspring", {"start": v(-73.63, 51.76) * mm, "mid": v(-80.2, 40.86) * mm, "end": v(-85.15, 29.14) * mm});
            skArc(sketch, "E109.trimOffspring", {"start": v(-54.03, 71.98) * mm, "mid": v(-63.64, 63.64) * mm, "end": v(-71.98, 54.03) * mm});
            skArc(sketch, "E110.trimOffspring", {"start": v(-29.14, 85.15) * mm, "mid": v(-40.86, 80.2) * mm, "end": v(-51.76, 73.63) * mm});
            skArc(sketch, "E111.trimOffspring", {"start": v(-1.4, 89.99) * mm, "mid": v(-14.08, 88.9) * mm, "end": v(-26.48, 86.02) * mm});
            skArc(sketch, "E112.trimOffspring", {"start": v(26.48, 86.02) * mm, "mid": v(14.08, 88.9) * mm, "end": v(1.4, 89.99) * mm});
            skArc(sketch, "E113.trimOffspring", {"start": v(51.76, 73.63) * mm, "mid": v(40.86, 80.2) * mm, "end": v(29.14, 85.15) * mm});
            skArc(sketch, "E114.trimOffspring", {"start": v(71.98, 54.03) * mm, "mid": v(63.64, 63.64) * mm, "end": v(54.03, 71.98) * mm});
            skArc(sketch, "E115.trimOffspring", {"start": v(85.15, 29.14) * mm, "mid": v(80.2, 40.86) * mm, "end": v(73.63, 51.76) * mm});
            skArc(sketch, "E116.trimOffspring", {"start": v(89.99, 1.4) * mm, "mid": v(88.9, 14.08) * mm, "end": v(86.02, 26.48) * mm});
            skArc(sketch, "E117.trimOffspring", {"start": v(86.02, -26.48) * mm, "mid": v(88.9, -14.08) * mm, "end": v(89.99, -1.4) * mm});
            skArc(sketch, "E118.trimOffspring", {"start": v(73.63, -51.76) * mm, "mid": v(80.2, -40.86) * mm, "end": v(85.15, -29.14) * mm});
            skArc(sketch, "E119.trimOffspring", {"start": v(54.03, -71.98) * mm, "mid": v(63.64, -63.64) * mm, "end": v(71.98, -54.03) * mm});
            skArc(sketch, "E120.trimOffspring", {"start": v(29.14, -85.15) * mm, "mid": v(40.86, -80.2) * mm, "end": v(51.76, -73.63) * mm});
            skArc(sketch, "E121.trimOffspring", {"start": v(1.4, -89.99) * mm, "mid": v(14.08, -88.9) * mm, "end": v(26.48, -86.02) * mm});
            skArc(sketch, "E122.trimOffspring", {"start": v(-26.48, -86.02) * mm, "mid": v(-14.08, -88.9) * mm, "end": v(-1.4, -89.99) * mm});
            skArc(sketch, "E123.trimOffspring", {"start": v(-51.76, -73.63) * mm, "mid": v(-40.86, -80.2) * mm, "end": v(-29.14, -85.15) * mm});
            skArc(sketch, "E124.trimOffspring", {"start": v(-71.98, -54.03) * mm, "mid": v(-63.64, -63.64) * mm, "end": v(-54.03, -71.98) * mm});
            skArc(sketch, "E125.trimOffspring", {"start": v(-85.15, -29.14) * mm, "mid": v(-80.2, -40.86) * mm, "end": v(-73.63, -51.76) * mm});
            skSolve(sketch);
        }
        {
            var Q0;
            Q0 = qSketchRegion(id + "F14", true);
            extrude(context, id + "F15", {"entities" : qUnion([Q0]), "depth" : 3 * mm});
        }
        {
            var Q0;
            Q0=qCreatedBy(id+"F4.planeOp",FACE);
            var sketch = newSketch(context, id + "F16", { "sketchPlane" : qUnion([Q0])});
            skCircle(sketch, "E126", {"center": v(0, 0) * mm, "radius": 95 * mm});
            skArc(sketch, "E127", {"start": v(-105, -1.4) * mm, "mid": v(-103.7, -16.43) * mm, "end": v(-100.28, -31.11) * mm});
            skLineSegment(sketch, "E128", {"start": v(-105, 1.4) * mm, "end": v(-102, 1.4) * mm});
            skLineSegment(sketch, "E129", {"start": v(-102, 1.4) * mm, "end": v(-102, -1.4) * mm});
            skLineSegment(sketch, "E130", {"start": v(-102, -1.4) * mm, "end": v(-105, -1.4) * mm});
            skLineSegment(sketch, "E131.1.0", {"start": v(-100.3, -31.12) * mm, "end": v(-97.44, -30.19) * mm});
            skLineSegment(sketch, "E131.1.1", {"start": v(-97.44, -30.19) * mm, "end": v(-96.58, -32.85) * mm});
            skLineSegment(sketch, "E131.1.2", {"start": v(-96.58, -32.85) * mm, "end": v(-99.43, -33.78) * mm});
            skLineSegment(sketch, "E131.2.0", {"start": v(-85.77, -60.58) * mm, "end": v(-83.34, -58.82) * mm});
            skLineSegment(sketch, "E131.2.1", {"start": v(-83.34, -58.82) * mm, "end": v(-81.7, -61.09) * mm});
            skLineSegment(sketch, "E131.2.2", {"start": v(-81.7, -61.09) * mm, "end": v(-84.12, -62.85) * mm});
            skLineSegment(sketch, "E131.3.0", {"start": v(-62.85, -84.12) * mm, "end": v(-61.09, -81.7) * mm});
            skLineSegment(sketch, "E131.3.1", {"start": v(-61.09, -81.7) * mm, "end": v(-58.82, -83.34) * mm});
            skLineSegment(sketch, "E131.3.2", {"start": v(-58.82, -83.34) * mm, "end": v(-60.58, -85.77) * mm});
            skLineSegment(sketch, "E131.4.0", {"start": v(-33.78, -99.43) * mm, "end": v(-32.85, -96.58) * mm});
            skLineSegment(sketch, "E131.4.1", {"start": v(-32.85, -96.58) * mm, "end": v(-30.19, -97.44) * mm});
            skLineSegment(sketch, "E131.4.2", {"start": v(-30.19, -97.44) * mm, "end": v(-31.12, -100.3) * mm});
            skLineSegment(sketch, "E131.5.0", {"start": v(-1.4, -105) * mm, "end": v(-1.4, -102) * mm});
            skLineSegment(sketch, "E131.5.1", {"start": v(-1.4, -102) * mm, "end": v(1.4, -102) * mm});
            skLineSegment(sketch, "E131.5.2", {"start": v(1.4, -102) * mm, "end": v(1.4, -105) * mm});
            skLineSegment(sketch, "E131.6.0", {"start": v(31.12, -100.3) * mm, "end": v(30.19, -97.44) * mm});
            skLineSegment(sketch, "E131.6.1", {"start": v(30.19, -97.44) * mm, "end": v(32.85, -96.58) * mm});
            skLineSegment(sketch, "E131.6.2", {"start": v(32.85, -96.58) * mm, "end": v(33.78, -99.43) * mm});
            skLineSegment(sketch, "E131.7.0", {"start": v(60.58, -85.77) * mm, "end": v(58.82, -83.34) * mm});
            skLineSegment(sketch, "E131.7.1", {"start": v(58.82, -83.34) * mm, "end": v(61.09, -81.7) * mm});
            skLineSegment(sketch, "E131.7.2", {"start": v(61.09, -81.7) * mm, "end": v(62.85, -84.12) * mm});
            skLineSegment(sketch, "E131.8.0", {"start": v(84.12, -62.85) * mm, "end": v(81.7, -61.09) * mm});
            skLineSegment(sketch, "E131.8.1", {"start": v(81.7, -61.09) * mm, "end": v(83.34, -58.82) * mm});
            skLineSegment(sketch, "E131.8.2", {"start": v(83.34, -58.82) * mm, "end": v(85.77, -60.58) * mm});
            skLineSegment(sketch, "E131.9.0", {"start": v(99.43, -33.78) * mm, "end": v(96.58, -32.85) * mm});
            skLineSegment(sketch, "E131.9.1", {"start": v(96.58, -32.85) * mm, "end": v(97.44, -30.19) * mm});
            skLineSegment(sketch, "E131.9.2", {"start": v(97.44, -30.19) * mm, "end": v(100.3, -31.12) * mm});
            skLineSegment(sketch, "E131.10.0", {"start": v(105, -1.4) * mm, "end": v(102, -1.4) * mm});
            skLineSegment(sketch, "E131.10.1", {"start": v(102, -1.4) * mm, "end": v(102, 1.4) * mm});
            skLineSegment(sketch, "E131.10.2", {"start": v(102, 1.4) * mm, "end": v(105, 1.4) * mm});
            skLineSegment(sketch, "E131.11.0", {"start": v(100.3, 31.12) * mm, "end": v(97.44, 30.19) * mm});
            skLineSegment(sketch, "E131.11.1", {"start": v(97.44, 30.19) * mm, "end": v(96.58, 32.85) * mm});
            skLineSegment(sketch, "E131.11.2", {"start": v(96.58, 32.85) * mm, "end": v(99.43, 33.78) * mm});
            skLineSegment(sketch, "E131.12.0", {"start": v(85.77, 60.58) * mm, "end": v(83.34, 58.82) * mm});
            skLineSegment(sketch, "E131.12.1", {"start": v(83.34, 58.82) * mm, "end": v(81.7, 61.09) * mm});
            skLineSegment(sketch, "E131.12.2", {"start": v(81.7, 61.09) * mm, "end": v(84.12, 62.85) * mm});
            skLineSegment(sketch, "E131.13.0", {"start": v(62.85, 84.12) * mm, "end": v(61.09, 81.7) * mm});
            skLineSegment(sketch, "E131.13.1", {"start": v(61.09, 81.7) * mm, "end": v(58.82, 83.34) * mm});
            skLineSegment(sketch, "E131.13.2", {"start": v(58.82, 83.34) * mm, "end": v(60.58, 85.77) * mm});
            skLineSegment(sketch, "E131.14.0", {"start": v(33.78, 99.43) * mm, "end": v(32.85, 96.58) * mm});
            skLineSegment(sketch, "E131.14.1", {"start": v(32.85, 96.58) * mm, "end": v(30.19, 97.44) * mm});
            skLineSegment(sketch, "E131.14.2", {"start": v(30.19, 97.44) * mm, "end": v(31.12, 100.3) * mm});
            skLineSegment(sketch, "E131.15.0", {"start": v(1.4, 105) * mm, "end": v(1.4, 102) * mm});
            skLineSegment(sketch, "E131.15.1", {"start": v(1.4, 102) * mm, "end": v(-1.4, 102) * mm});
            skLineSegment(sketch, "E131.15.2", {"start": v(-1.4, 102) * mm, "end": v(-1.4, 105) * mm});
            skLineSegment(sketch, "E131.16.0", {"start": v(-31.12, 100.3) * mm, "end": v(-30.19, 97.44) * mm});
            skLineSegment(sketch, "E131.16.1", {"start": v(-30.19, 97.44) * mm, "end": v(-32.85, 96.58) * mm});
            skLineSegment(sketch, "E131.16.2", {"start": v(-32.85, 96.58) * mm, "end": v(-33.78, 99.43) * mm});
            skLineSegment(sketch, "E131.17.0", {"start": v(-60.58, 85.77) * mm, "end": v(-58.82, 83.34) * mm});
            skLineSegment(sketch, "E131.17.1", {"start": v(-58.82, 83.34) * mm, "end": v(-61.09, 81.7) * mm});
            skLineSegment(sketch, "E131.17.2", {"start": v(-61.09, 81.7) * mm, "end": v(-62.85, 84.12) * mm});
            skLineSegment(sketch, "E131.18.0", {"start": v(-84.12, 62.85) * mm, "end": v(-81.7, 61.09) * mm});
            skLineSegment(sketch, "E131.18.1", {"start": v(-81.7, 61.09) * mm, "end": v(-83.34, 58.82) * mm});
            skLineSegment(sketch, "E131.18.2", {"start": v(-83.34, 58.82) * mm, "end": v(-85.77, 60.58) * mm});
            skLineSegment(sketch, "E131.19.0", {"start": v(-99.43, 33.78) * mm, "end": v(-96.58, 32.85) * mm});
            skLineSegment(sketch, "E131.19.1", {"start": v(-96.58, 32.85) * mm, "end": v(-97.44, 30.19) * mm});
            skLineSegment(sketch, "E131.19.2", {"start": v(-97.44, 30.19) * mm, "end": v(-100.3, 31.12) * mm});
            skArc(sketch, "E132.trimOffspring", {"start": v(-100.28, 31.11) * mm, "mid": v(-103.7, 16.43) * mm, "end": v(-105, 1.4) * mm});
            skArc(sketch, "E133.trimOffspring", {"start": v(-85.76, 60.58) * mm, "mid": v(-93.56, 47.67) * mm, "end": v(-99.42, 33.78) * mm});
            skArc(sketch, "E134.trimOffspring", {"start": v(-62.84, 84.12) * mm, "mid": v(-74.25, 74.25) * mm, "end": v(-84.12, 62.84) * mm});
            skArc(sketch, "E135.trimOffspring", {"start": v(-33.78, 99.42) * mm, "mid": v(-47.67, 93.56) * mm, "end": v(-60.58, 85.76) * mm});
            skArc(sketch, "E136.trimOffspring", {"start": v(-1.4, 105) * mm, "mid": v(-16.43, 103.7) * mm, "end": v(-31.11, 100.28) * mm});
            skArc(sketch, "E137.trimOffspring", {"start": v(31.11, 100.28) * mm, "mid": v(16.43, 103.7) * mm, "end": v(1.4, 105) * mm});
            skArc(sketch, "E138.trimOffspring", {"start": v(60.58, 85.76) * mm, "mid": v(47.67, 93.56) * mm, "end": v(33.78, 99.42) * mm});
            skArc(sketch, "E139.trimOffspring", {"start": v(84.12, 62.84) * mm, "mid": v(74.25, 74.25) * mm, "end": v(62.84, 84.12) * mm});
            skArc(sketch, "E140.trimOffspring", {"start": v(99.42, 33.78) * mm, "mid": v(93.56, 47.67) * mm, "end": v(85.76, 60.58) * mm});
            skArc(sketch, "E141.trimOffspring", {"start": v(105, 1.4) * mm, "mid": v(103.7, 16.43) * mm, "end": v(100.28, 31.11) * mm});
            skArc(sketch, "E142.trimOffspring", {"start": v(100.28, -31.11) * mm, "mid": v(103.7, -16.43) * mm, "end": v(105, -1.4) * mm});
            skArc(sketch, "E143.trimOffspring", {"start": v(85.76, -60.58) * mm, "mid": v(93.56, -47.67) * mm, "end": v(99.42, -33.78) * mm});
            skArc(sketch, "E144.trimOffspring", {"start": v(62.84, -84.12) * mm, "mid": v(74.25, -74.25) * mm, "end": v(84.12, -62.84) * mm});
            skArc(sketch, "E145.trimOffspring", {"start": v(33.78, -99.42) * mm, "mid": v(47.67, -93.56) * mm, "end": v(60.58, -85.76) * mm});
            skArc(sketch, "E146.trimOffspring", {"start": v(1.4, -105) * mm, "mid": v(16.43, -103.7) * mm, "end": v(31.11, -100.28) * mm});
            skArc(sketch, "E147.trimOffspring", {"start": v(-31.11, -100.28) * mm, "mid": v(-16.43, -103.7) * mm, "end": v(-1.4, -105) * mm});
            skArc(sketch, "E148.trimOffspring", {"start": v(-60.58, -85.76) * mm, "mid": v(-47.67, -93.56) * mm, "end": v(-33.78, -99.42) * mm});
            skArc(sketch, "E149.trimOffspring", {"start": v(-84.12, -62.84) * mm, "mid": v(-74.25, -74.25) * mm, "end": v(-62.84, -84.12) * mm});
            skArc(sketch, "E150.trimOffspring", {"start": v(-99.42, -33.78) * mm, "mid": v(-93.56, -47.67) * mm, "end": v(-85.76, -60.58) * mm});
            skSolve(sketch);
        }
        {
            var Q0;
            Q0 = qSketchRegion(id + "F16", true);
            extrude(context, id + "F17", {"entities" : qUnion([Q0]), "depth" : 3 * mm});
        }
        {
            var Q0;
            Q0=qCreatedBy(id+"F5.planeOp",FACE);
            var sketch = newSketch(context, id + "F18", { "sketchPlane" : qUnion([Q0])});
            skCircle(sketch, "E151", {"center": v(0, 0) * mm, "radius": 95 * mm});
            skArc(sketch, "E152", {"start": v(-105, -1.4) * mm, "mid": v(-103.7, -16.43) * mm, "end": v(-100.28, -31.11) * mm});
            skLineSegment(sketch, "E153", {"start": v(-105, 1.4) * mm, "end": v(-102, 1.4) * mm});
            skLineSegment(sketch, "E154", {"start": v(-102, 1.4) * mm, "end": v(-102, -1.4) * mm});
            skLineSegment(sketch, "E155", {"start": v(-102, -1.4) * mm, "end": v(-105, -1.4) * mm});
            skLineSegment(sketch, "E156.1.0", {"start": v(-97.44, -30.19) * mm, "end": v(-96.58, -32.85) * mm});
            skLineSegment(sketch, "E156.1.1", {"start": v(-100.3, -31.12) * mm, "end": v(-97.44, -30.19) * mm});
            skLineSegment(sketch, "E156.1.2", {"start": v(-96.58, -32.85) * mm, "end": v(-99.43, -33.78) * mm});
            skLineSegment(sketch, "E156.2.0", {"start": v(-83.34, -58.82) * mm, "end": v(-81.7, -61.09) * mm});
            skLineSegment(sketch, "E156.2.1", {"start": v(-85.77, -60.58) * mm, "end": v(-83.34, -58.82) * mm});
            skLineSegment(sketch, "E156.2.2", {"start": v(-81.7, -61.09) * mm, "end": v(-84.12, -62.85) * mm});
            skLineSegment(sketch, "E156.3.0", {"start": v(-61.09, -81.7) * mm, "end": v(-58.82, -83.34) * mm});
            skLineSegment(sketch, "E156.3.1", {"start": v(-62.85, -84.12) * mm, "end": v(-61.09, -81.7) * mm});
            skLineSegment(sketch, "E156.3.2", {"start": v(-58.82, -83.34) * mm, "end": v(-60.58, -85.77) * mm});
            skLineSegment(sketch, "E156.4.0", {"start": v(-32.85, -96.58) * mm, "end": v(-30.19, -97.44) * mm});
            skLineSegment(sketch, "E156.4.1", {"start": v(-33.78, -99.43) * mm, "end": v(-32.85, -96.58) * mm});
            skLineSegment(sketch, "E156.4.2", {"start": v(-30.19, -97.44) * mm, "end": v(-31.12, -100.3) * mm});
            skLineSegment(sketch, "E156.5.0", {"start": v(-1.4, -102) * mm, "end": v(1.4, -102) * mm});
            skLineSegment(sketch, "E156.5.1", {"start": v(-1.4, -105) * mm, "end": v(-1.4, -102) * mm});
            skLineSegment(sketch, "E156.5.2", {"start": v(1.4, -102) * mm, "end": v(1.4, -105) * mm});
            skLineSegment(sketch, "E156.6.0", {"start": v(30.19, -97.44) * mm, "end": v(32.85, -96.58) * mm});
            skLineSegment(sketch, "E156.6.1", {"start": v(31.12, -100.3) * mm, "end": v(30.19, -97.44) * mm});
            skLineSegment(sketch, "E156.6.2", {"start": v(32.85, -96.58) * mm, "end": v(33.78, -99.43) * mm});
            skLineSegment(sketch, "E156.7.0", {"start": v(58.82, -83.34) * mm, "end": v(61.09, -81.7) * mm});
            skLineSegment(sketch, "E156.7.1", {"start": v(60.58, -85.77) * mm, "end": v(58.82, -83.34) * mm});
            skLineSegment(sketch, "E156.7.2", {"start": v(61.09, -81.7) * mm, "end": v(62.85, -84.12) * mm});
            skLineSegment(sketch, "E156.8.0", {"start": v(81.7, -61.09) * mm, "end": v(83.34, -58.82) * mm});
            skLineSegment(sketch, "E156.8.1", {"start": v(84.12, -62.85) * mm, "end": v(81.7, -61.09) * mm});
            skLineSegment(sketch, "E156.8.2", {"start": v(83.34, -58.82) * mm, "end": v(85.77, -60.58) * mm});
            skLineSegment(sketch, "E156.9.0", {"start": v(96.58, -32.85) * mm, "end": v(97.44, -30.19) * mm});
            skLineSegment(sketch, "E156.9.1", {"start": v(99.43, -33.78) * mm, "end": v(96.58, -32.85) * mm});
            skLineSegment(sketch, "E156.9.2", {"start": v(97.44, -30.19) * mm, "end": v(100.3, -31.12) * mm});
            skLineSegment(sketch, "E156.10.0", {"start": v(102, -1.4) * mm, "end": v(102, 1.4) * mm});
            skLineSegment(sketch, "E156.10.1", {"start": v(105, -1.4) * mm, "end": v(102, -1.4) * mm});
            skLineSegment(sketch, "E156.10.2", {"start": v(102, 1.4) * mm, "end": v(105, 1.4) * mm});
            skLineSegment(sketch, "E156.11.0", {"start": v(97.44, 30.19) * mm, "end": v(96.58, 32.85) * mm});
            skLineSegment(sketch, "E156.11.1", {"start": v(100.3, 31.12) * mm, "end": v(97.44, 30.19) * mm});
            skLineSegment(sketch, "E156.11.2", {"start": v(96.58, 32.85) * mm, "end": v(99.43, 33.78) * mm});
            skLineSegment(sketch, "E156.12.0", {"start": v(83.34, 58.82) * mm, "end": v(81.7, 61.09) * mm});
            skLineSegment(sketch, "E156.12.1", {"start": v(85.77, 60.58) * mm, "end": v(83.34, 58.82) * mm});
            skLineSegment(sketch, "E156.12.2", {"start": v(81.7, 61.09) * mm, "end": v(84.12, 62.85) * mm});
            skLineSegment(sketch, "E156.13.0", {"start": v(61.09, 81.7) * mm, "end": v(58.82, 83.34) * mm});
            skLineSegment(sketch, "E156.13.1", {"start": v(62.85, 84.12) * mm, "end": v(61.09, 81.7) * mm});
            skLineSegment(sketch, "E156.13.2", {"start": v(58.82, 83.34) * mm, "end": v(60.58, 85.77) * mm});
            skLineSegment(sketch, "E156.14.0", {"start": v(32.85, 96.58) * mm, "end": v(30.19, 97.44) * mm});
            skLineSegment(sketch, "E156.14.1", {"start": v(33.78, 99.43) * mm, "end": v(32.85, 96.58) * mm});
            skLineSegment(sketch, "E156.14.2", {"start": v(30.19, 97.44) * mm, "end": v(31.12, 100.3) * mm});
            skLineSegment(sketch, "E156.15.0", {"start": v(1.4, 102) * mm, "end": v(-1.4, 102) * mm});
            skLineSegment(sketch, "E156.15.1", {"start": v(1.4, 105) * mm, "end": v(1.4, 102) * mm});
            skLineSegment(sketch, "E156.15.2", {"start": v(-1.4, 102) * mm, "end": v(-1.4, 105) * mm});
            skLineSegment(sketch, "E156.16.0", {"start": v(-30.19, 97.44) * mm, "end": v(-32.85, 96.58) * mm});
            skLineSegment(sketch, "E156.16.1", {"start": v(-31.12, 100.3) * mm, "end": v(-30.19, 97.44) * mm});
            skLineSegment(sketch, "E156.16.2", {"start": v(-32.85, 96.58) * mm, "end": v(-33.78, 99.43) * mm});
            skLineSegment(sketch, "E156.17.0", {"start": v(-58.82, 83.34) * mm, "end": v(-61.09, 81.7) * mm});
            skLineSegment(sketch, "E156.17.1", {"start": v(-60.58, 85.77) * mm, "end": v(-58.82, 83.34) * mm});
            skLineSegment(sketch, "E156.17.2", {"start": v(-61.09, 81.7) * mm, "end": v(-62.85, 84.12) * mm});
            skLineSegment(sketch, "E156.18.0", {"start": v(-81.7, 61.09) * mm, "end": v(-83.34, 58.82) * mm});
            skLineSegment(sketch, "E156.18.1", {"start": v(-84.12, 62.85) * mm, "end": v(-81.7, 61.09) * mm});
            skLineSegment(sketch, "E156.18.2", {"start": v(-83.34, 58.82) * mm, "end": v(-85.77, 60.58) * mm});
            skLineSegment(sketch, "E156.19.0", {"start": v(-96.58, 32.85) * mm, "end": v(-97.44, 30.19) * mm});
            skLineSegment(sketch, "E156.19.1", {"start": v(-99.43, 33.78) * mm, "end": v(-96.58, 32.85) * mm});
            skLineSegment(sketch, "E156.19.2", {"start": v(-97.44, 30.19) * mm, "end": v(-100.3, 31.12) * mm});
            skArc(sketch, "E157.trimOffspring", {"start": v(-100.28, 31.11) * mm, "mid": v(-103.7, 16.43) * mm, "end": v(-105, 1.4) * mm});
            skArc(sketch, "E158.trimOffspring", {"start": v(-85.76, 60.58) * mm, "mid": v(-93.56, 47.67) * mm, "end": v(-99.42, 33.78) * mm});
            skArc(sketch, "E159.trimOffspring", {"start": v(-62.84, 84.12) * mm, "mid": v(-74.25, 74.25) * mm, "end": v(-84.12, 62.84) * mm});
            skArc(sketch, "E160.trimOffspring", {"start": v(-33.78, 99.42) * mm, "mid": v(-47.67, 93.56) * mm, "end": v(-60.58, 85.76) * mm});
            skArc(sketch, "E161.trimOffspring", {"start": v(-1.4, 105) * mm, "mid": v(-16.43, 103.7) * mm, "end": v(-31.11, 100.28) * mm});
            skArc(sketch, "E162.trimOffspring", {"start": v(31.11, 100.28) * mm, "mid": v(16.43, 103.7) * mm, "end": v(1.4, 105) * mm});
            skArc(sketch, "E163.trimOffspring", {"start": v(60.58, 85.76) * mm, "mid": v(47.67, 93.56) * mm, "end": v(33.78, 99.42) * mm});
            skArc(sketch, "E164.trimOffspring", {"start": v(84.12, 62.84) * mm, "mid": v(74.25, 74.25) * mm, "end": v(62.84, 84.12) * mm});
            skArc(sketch, "E165.trimOffspring", {"start": v(99.42, 33.78) * mm, "mid": v(93.56, 47.67) * mm, "end": v(85.76, 60.58) * mm});
            skArc(sketch, "E166.trimOffspring", {"start": v(105, 1.4) * mm, "mid": v(103.7, 16.43) * mm, "end": v(100.28, 31.11) * mm});
            skArc(sketch, "E167.trimOffspring", {"start": v(100.28, -31.11) * mm, "mid": v(103.7, -16.43) * mm, "end": v(105, -1.4) * mm});
            skArc(sketch, "E168.trimOffspring", {"start": v(85.76, -60.58) * mm, "mid": v(93.56, -47.67) * mm, "end": v(99.42, -33.78) * mm});
            skArc(sketch, "E169.trimOffspring", {"start": v(62.84, -84.12) * mm, "mid": v(74.25, -74.25) * mm, "end": v(84.12, -62.84) * mm});
            skArc(sketch, "E170.trimOffspring", {"start": v(33.78, -99.42) * mm, "mid": v(47.67, -93.56) * mm, "end": v(60.58, -85.76) * mm});
            skArc(sketch, "E171.trimOffspring", {"start": v(1.4, -105) * mm, "mid": v(16.43, -103.7) * mm, "end": v(31.11, -100.28) * mm});
            skArc(sketch, "E172.trimOffspring", {"start": v(-31.11, -100.28) * mm, "mid": v(-16.43, -103.7) * mm, "end": v(-1.4, -105) * mm});
            skArc(sketch, "E173.trimOffspring", {"start": v(-60.58, -85.76) * mm, "mid": v(-47.67, -93.56) * mm, "end": v(-33.78, -99.42) * mm});
            skArc(sketch, "E174.trimOffspring", {"start": v(-84.12, -62.84) * mm, "mid": v(-74.25, -74.25) * mm, "end": v(-62.84, -84.12) * mm});
            skArc(sketch, "E175.trimOffspring", {"start": v(-99.42, -33.78) * mm, "mid": v(-93.56, -47.67) * mm, "end": v(-85.76, -60.58) * mm});
            skSolve(sketch);
        }
        {
            var Q0;
            Q0 = qSketchRegion(id + "F18", true);
            extrude(context, id + "F19", {"entities" : qUnion([Q0]), "depth" : 3 * mm});
        }
        {
            var Q0;
            Q0=qCreatedBy(makeId("Front.planeOp"),FACE);
            var sketch = newSketch(context, id + "F20", { "sketchPlane" : qUnion([Q0])});
            skPoint(sketch, "E176.orphan", {"position": v(0, -133.1) * mm});
            skLineSegment(sketch, "E177", {"start": v(-39, 163) * mm, "end": v(-39, 152.8) * mm});
            skLineSegment(sketch, "E178", {"start": v(0, 212.36) * mm, "end": v(0, -226.97) * mm, "construction": true});
            skLineSegment(sketch, "E179", {"start": v(-39, 100) * mm, "end": v(-53.16, 52.8) * mm});
            skLineSegment(sketch, "E180", {"start": v(-109, -100) * mm, "end": v(-49, 100) * mm});
            skLineSegment(sketch, "E181", {"start": v(-49, 100) * mm, "end": v(-49, 158) * mm});
            skLineSegment(sketch, "E182", {"start": v(-44, 163) * mm, "end": v(-39, 163) * mm});
            skLineSegment(sketch, "E183", {"start": v(-99, -100) * mm, "end": v(-99, -147.2) * mm});
            skLineSegment(sketch, "E184", {"start": v(-109, -100) * mm, "end": v(-109, -155) * mm});
            skLineSegment(sketch, "E185", {"start": v(-104, -160) * mm, "end": v(-99, -160) * mm});
            skPoint(sketch, "E186.visualSharp", {"position": v(-109, -160) * mm});
            skArc(sketch, "E186.filletArc", {"start": v(-109, -155) * mm, "mid": v(-107.54, -158.54) * mm, "end": v(-104, -160) * mm});
            skPoint(sketch, "E187.visualSharp", {"position": v(-49, 163) * mm});
            skArc(sketch, "E187.filletArc", {"start": v(-44, 163) * mm, "mid": v(-47.54, 161.54) * mm, "end": v(-49, 158) * mm});
            skLineSegment(sketch, "E188", {"start": v(-39, 152.8) * mm, "end": v(-42, 152.8) * mm});
            skLineSegment(sketch, "E189", {"start": v(-42, 152.8) * mm, "end": v(-42, 150) * mm});
            skLineSegment(sketch, "E190", {"start": v(-42, 150) * mm, "end": v(-39, 150) * mm});
            skLineSegment(sketch, "E191.trimOffspring", {"start": v(-39, 150) * mm, "end": v(-39, 102.8) * mm});
            skLineSegment(sketch, "E192", {"start": v(-39, 102.8) * mm, "end": v(-42, 102.8) * mm});
            skLineSegment(sketch, "E193", {"start": v(-42, 102.8) * mm, "end": v(-42, 100) * mm});
            skLineSegment(sketch, "E194", {"start": v(-42, 100) * mm, "end": v(-39, 100) * mm});
            skLineSegment(sketch, "E195", {"start": v(-99, -147.2) * mm, "end": v(-102, -147.2) * mm});
            skLineSegment(sketch, "E196", {"start": v(-102, -147.2) * mm, "end": v(-102, -150) * mm});
            skLineSegment(sketch, "E197", {"start": v(-102, -150) * mm, "end": v(-99, -150) * mm});
            skLineSegment(sketch, "E198", {"start": v(-53.16, 52.8) * mm, "end": v(-57, 52.8) * mm});
            skLineSegment(sketch, "E199", {"start": v(-57, 52.8) * mm, "end": v(-57, 50) * mm});
            skLineSegment(sketch, "E200", {"start": v(-57, 50) * mm, "end": v(-54, 50) * mm});
            skLineSegment(sketch, "E201.trimOffspring", {"start": v(-54, 50) * mm, "end": v(-68.16, 2.8) * mm});
            skLineSegment(sketch, "E202", {"start": v(-102, -97.2) * mm, "end": v(-102, -100) * mm});
            skLineSegment(sketch, "E203", {"start": v(-102, -100) * mm, "end": v(-99, -100) * mm});
            skLineSegment(sketch, "E204", {"start": v(-68.16, 2.8) * mm, "end": v(-72, 2.8) * mm});
            skLineSegment(sketch, "E205", {"start": v(-72, 2.8) * mm, "end": v(-72, 0) * mm});
            skLineSegment(sketch, "E206", {"start": v(-72, 0) * mm, "end": v(-69, 0) * mm});
            skLineSegment(sketch, "E207.trimOffspring", {"start": v(-69, 0) * mm, "end": v(-83.16, -47.2) * mm});
            skLineSegment(sketch, "E208", {"start": v(-83.16, -47.2) * mm, "end": v(-87, -47.2) * mm});
            skLineSegment(sketch, "E209", {"start": v(-87, -47.2) * mm, "end": v(-87, -50) * mm});
            skLineSegment(sketch, "E210", {"start": v(-87, -50) * mm, "end": v(-84, -50) * mm});
            skLineSegment(sketch, "E211.trimOffspring", {"start": v(-84, -50) * mm, "end": v(-98.16, -97.2) * mm});
            skLineSegment(sketch, "E212", {"start": v(-102, -97.2) * mm, "end": v(-98.16, -97.2) * mm});
            skLineSegment(sketch, "E213.trimOffspring", {"start": v(-99, -150) * mm, "end": v(-99, -160) * mm});
            skSolve(sketch);
        }
        {
            var Q0;
            Q0 = qSketchRegion(id + "F20", true);
            extrude(context, id + "F21", {"entities" : qUnion([Q0]), "endBound" : BoundingType.SYMMETRIC, "depth" : 3 * mm});
        }
        {
            var Q0;
            Q0=makeQuery(id+"F21.opExtrude","SWEPT_BODY",BODY,{"disambiguationData":[OSD([sQuery(id+"F20.wireOp",EDGE,"E177"),sQuery(id+"F20.wireOp",EDGE,"E179"),sQuery(id+"F20.wireOp",EDGE,"qeIH5ldY-Qqop-Qkw5-p5GL-fOUBYGfcbpAQ"),sQuery(id+"F20.wireOp",EDGE,"PqXnasbW-HfTa-s4Ih-XuKP-vwoH3OxkAbOH"),sQuery(id+"F20.wireOp",EDGE,"jecK3vyC-5IsW-QCA9-NphO-Yhlttf9JcoDM"),sQuery(id+"F20.wireOp",EDGE,"E180"),sQuery(id+"F20.wireOp",EDGE,"E181"),sQuery(id+"F20.wireOp",EDGE,"E182")])]});
            var Q1;
            Q1=makeQuery(id+"F13.opExtrude","CAP_EDGE",EDGE,{"disambiguationData":[OSD([sQuery(id+"F12.wireOp",EDGE,"E76")])],"isStart":false});
            circularPattern(context, id + "F22", {"entities" : qUnion([Q0]), "axis" : qUnion([Q1]), "angle" : 360 * degree, "instanceCount" : 20, "equalSpace" : true});
        }
    });
